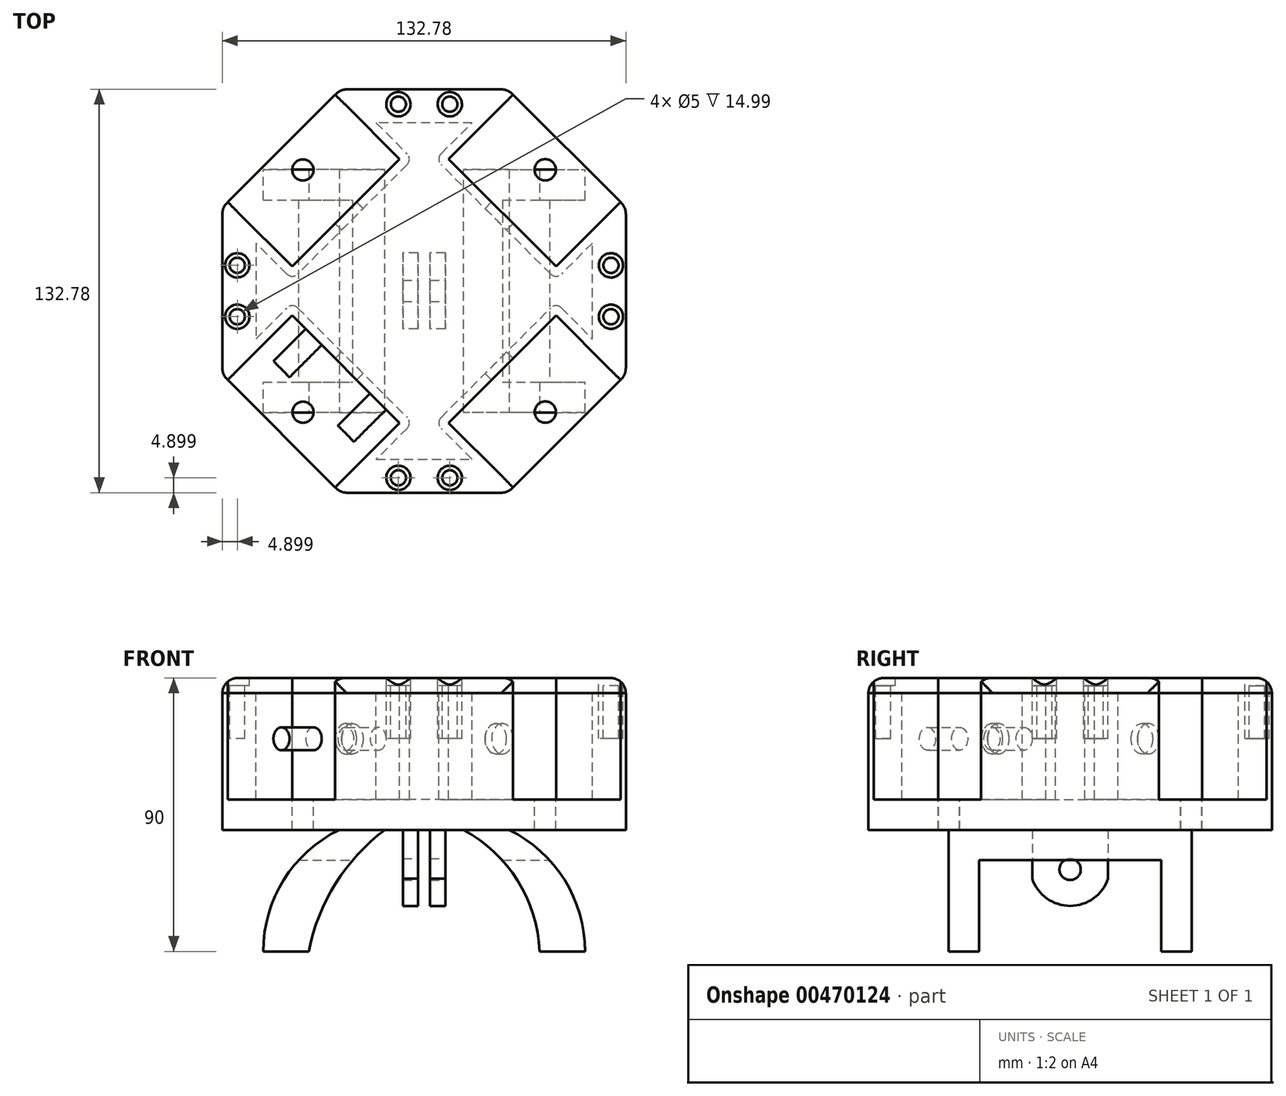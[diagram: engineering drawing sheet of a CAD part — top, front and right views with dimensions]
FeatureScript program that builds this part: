
annotation { "Feature Type Name" : "Feature", "Feature Type Description" : "" }
export const myFeature = defineFeature(function(context is Context, id is Id, definition is map)
    precondition{}
    {
        {
            var Q0;
            Q0=qCreatedBy(makeId("Top.planeOp"),FACE);
            var sketch = newSketch(context, id + "F0", { "sketchPlane" : qUnion([Q0])});
            skCircle(sketch, "E0.cCircle", {"center": v(0, 0) * mm, "radius": 71.86 * mm, "construction": true});
            skLineSegment(sketch, "E0.0", {"start": v(66.4, 27.5) * mm, "end": v(66.4, -27.5) * mm});
            skLineSegment(sketch, "E0.1", {"start": v(66.4, -27.5) * mm, "end": v(27.5, -66.4) * mm});
            skLineSegment(sketch, "E0.2", {"start": v(27.5, -66.4) * mm, "end": v(-27.5, -66.4) * mm});
            skLineSegment(sketch, "E0.3", {"start": v(-27.5, -66.4) * mm, "end": v(-66.4, -27.5) * mm});
            skLineSegment(sketch, "E0.4", {"start": v(-66.4, -27.5) * mm, "end": v(-66.4, 27.5) * mm});
            skLineSegment(sketch, "E0.5", {"start": v(-66.4, 27.5) * mm, "end": v(-27.5, 66.4) * mm});
            skLineSegment(sketch, "E0.6", {"start": v(-27.5, 66.4) * mm, "end": v(27.5, 66.4) * mm});
            skLineSegment(sketch, "E0.7", {"start": v(27.5, 66.4) * mm, "end": v(66.4, 27.5) * mm});
            skSolve(sketch);
        }
        {
            var Q0;
            Q0=makeQuery(id+"F0.imprint","IMPRINT",FACE,{"disambiguationData":[TD([[makeQuery(id+"F0.imprint","IMPRINT",EDGE,{"derivedFrom":sQuery(id+"F0.wireOp",EDGE,"E0.0")}),-1.0]])]});
            extrude(context, id + "F1", {"entities" : qUnion([Q0]), "depth" : 50 * mm});
        }
        {
            var Q0;
            Q0=makeQuery(id+"F1.opExtrude","CAP_FACE",FACE,{"disambiguationData":[OSD([sQuery(id+"F0.wireOp",EDGE,"E0.0"),sQuery(id+"F0.wireOp",EDGE,"E0.1"),sQuery(id+"F0.wireOp",EDGE,"E0.2"),sQuery(id+"F0.wireOp",EDGE,"E0.3"),sQuery(id+"F0.wireOp",EDGE,"E0.4"),sQuery(id+"F0.wireOp",EDGE,"E0.5"),sQuery(id+"F0.wireOp",EDGE,"E0.6"),sQuery(id+"F0.wireOp",EDGE,"E0.7")])],"isStart":true});
            var sketch = newSketch(context, id + "F2", { "sketchPlane" : qUnion([Q0])});
            skLineSegment(sketch, "E1", {"start": v(0, 66.4) * mm, "end": v(0, -66.4) * mm});
            skLineSegment(sketch, "E2.bottom", {"start": v(52.96, 40) * mm, "end": v(12.96, 40) * mm});
            skLineSegment(sketch, "E2.top", {"start": v(52.96, -40) * mm, "end": v(12.96, -40) * mm});
            skLineSegment(sketch, "E2.left", {"start": v(52.96, 40) * mm, "end": v(52.96, -40) * mm});
            skLineSegment(sketch, "E2.right", {"start": v(12.96, 40) * mm, "end": v(12.96, -40) * mm});
            skPoint(sketch, "E2.middle", {"position": v(32.96, 0) * mm});
            skLineSegment(sketch, "E3.MirrorCS", {"start": v(-12.96, 40) * mm, "end": v(-12.96, -40) * mm});
            skLineSegment(sketch, "E4.MirrorCS", {"start": v(-52.96, 40) * mm, "end": v(-12.96, 40) * mm});
            skLineSegment(sketch, "E5.MirrorCS", {"start": v(-52.96, 40) * mm, "end": v(-52.96, -40) * mm});
            skLineSegment(sketch, "E6.MirrorCS", {"start": v(-52.96, -40) * mm, "end": v(-12.96, -40) * mm});
            skSolve(sketch);
        }
        {
            var Q0;
            Q0 = qSketchRegion(id + "F2", true);
            extrude(context, id + "F3", {"entities" : qUnion([Q0]), "operationType" : NewBodyOperationType.ADD, "depth" : 40 * mm});
        }
        {
            var Q0;
            Q0=makeQuery(id+"F3.opExtrude","SWEPT_FACE",FACE,{"disambiguationData":[OSD([sQuery(id+"F2.wireOp",EDGE,"E2.bottom")])]});
            var sketch = newSketch(context, id + "F4", { "sketchPlane" : qUnion([Q0])});
            skArc(sketch, "E7", {"start": v(52.96, -40) * mm, "mid": v(46.2, -16.42) * mm, "end": v(27.96, 0) * mm});
            skArc(sketch, "E8", {"start": v(37.96, -40) * mm, "mid": v(30.79, -16.67) * mm, "end": v(12.96, 0) * mm});
            skLineSegment(sketch, "E9", {"start": v(0, 0) * mm, "end": v(0, -51.15) * mm});
            skArc(sketch, "E10.MirrorCS", {"start": v(-37.96, -40) * mm, "mid": v(-30.79, -16.67) * mm, "end": v(-12.96, 0) * mm});
            skArc(sketch, "E11.MirrorCS", {"start": v(-52.96, -40) * mm, "mid": v(-46.2, -16.42) * mm, "end": v(-27.96, 0) * mm});
            skLineSegment(sketch, "E12", {"start": v(-37.96, -40) * mm, "end": v(-52.96, -40) * mm});
            skLineSegment(sketch, "E13", {"start": v(-27.96, 0) * mm, "end": v(-12.96, 0) * mm});
            skSolve(sketch);
        }
        {
            var Q0;
            {var subQ0=sQuery(id+"F4.wireOp",EDGE,"E7");Q0=makeQuery(id+"F4.imprint","IMPRINT",FACE,{"disambiguationData":[TD([[makeQuery(id+"F4.imprint","IMPRINT",EDGE,{"derivedFrom":subQ0}),-1.0]])]});}
            var Q1;
            {var subQ0=sQuery(id+"F4.wireOp",EDGE,"E8");Q1=makeQuery(id+"F4.imprint","IMPRINT",FACE,{"disambiguationData":[TD([[makeQuery(id+"F4.imprint","IMPRINT",EDGE,{"derivedFrom":subQ0}),1.0]])]});}
            extrude(context, id + "F5", {"entities" : qUnion([Q0, Q1]), "operationType" : NewBodyOperationType.REMOVE, "endBound" : BoundingType.THROUGH_ALL, "oppositeDirection" : true, "depth" : 25 * mm});
        }
        {
            var Q0;
            Q0=makeQuery(id+"F3.opExtrude","SWEPT_FACE",FACE,{"disambiguationData":[OSD([sQuery(id+"F2.wireOp",EDGE,"E4.MirrorCS")])]});
            var sketch = newSketch(context, id + "F6", { "sketchPlane" : qUnion([Q0])});
            skArc(sketch, "E14", {"start": v(-27.96, 0) * mm, "mid": v(-46.2, -16.42) * mm, "end": v(-52.96, -40) * mm});
            skArc(sketch, "E15", {"start": v(-12.96, 0) * mm, "mid": v(-29.15, -17.7) * mm, "end": v(-37.96, -40) * mm});
            skSolve(sketch);
        }
        {
            var Q0;
            {var subQ0=sQuery(id+"F6.wireOp",EDGE,"E15");Q0=makeQuery(id+"F6.imprint","IMPRINT",FACE,{"disambiguationData":[TD([[makeQuery(id+"F6.imprint","IMPRINT",EDGE,{"derivedFrom":subQ0}),1.0]])]});}
            var Q1;
            {var subQ0=sQuery(id+"F6.wireOp",EDGE,"E14");Q1=makeQuery(id+"F6.imprint","IMPRINT",FACE,{"disambiguationData":[TD([[makeQuery(id+"F6.imprint","IMPRINT",EDGE,{"derivedFrom":subQ0}),-1.0]])]});}
            extrude(context, id + "F7", {"entities" : qUnion([Q0, Q1]), "operationType" : NewBodyOperationType.REMOVE, "endBound" : BoundingType.THROUGH_ALL, "oppositeDirection" : true, "depth" : 25 * mm});
        }
        {
            var Q0;
            Q0=makeQuery(id+"F3.opExtrude","CAP_FACE",FACE,{"disambiguationData":[OSD([sQuery(id+"F2.wireOp",EDGE,"E2.bottom"),sQuery(id+"F2.wireOp",EDGE,"E2.top"),sQuery(id+"F2.wireOp",EDGE,"E2.left"),sQuery(id+"F2.wireOp",EDGE,"E2.right")])],"isStart":false});
            extrude(context, id + "F8", {"entities" : qUnion([Q0]), "operationType" : NewBodyOperationType.ADD, "depth" : 10 * mm});
        }
        {
            var Q0;
            Q0=makeQuery(id+"F8.opExtrude","SWEPT_FACE",FACE,{"disambiguationData":[OSD([sQuery(id+"F2.wireOp",EDGE,"E2.bottom"),sQuery(id+"F2.wireOp",EDGE,"E2.left"),sQuery(id+"F4.wireOp",EDGE,"E7")])]});
            var sketch = newSketch(context, id + "F9", { "sketchPlane" : qUnion([Q0])});
            skLineSegment(sketch, "E16.bottom", {"start": v(-30, -50) * mm, "end": v(30, -50) * mm});
            skLineSegment(sketch, "E16.top", {"start": v(-30, -10) * mm, "end": v(30, -10) * mm});
            skLineSegment(sketch, "E16.left", {"start": v(-30, -50) * mm, "end": v(-30, -10) * mm});
            skLineSegment(sketch, "E16.right", {"start": v(30, -50) * mm, "end": v(30, -10) * mm});
            skLineSegment(sketch, "E17.bottom", {"start": v(-40, -40) * mm, "end": v(40, -40) * mm});
            skLineSegment(sketch, "E17.top", {"start": v(-40, -50) * mm, "end": v(40, -50) * mm});
            skLineSegment(sketch, "E17.left", {"start": v(-40, -40) * mm, "end": v(-40, -50) * mm});
            skLineSegment(sketch, "E17.right", {"start": v(40, -40) * mm, "end": v(40, -50) * mm});
            skSolve(sketch);
        }
        {
            var Q0;
            Q0 = qSketchRegion(id + "F9", true);
            extrude(context, id + "F10", {"entities" : qUnion([Q0]), "operationType" : NewBodyOperationType.REMOVE, "endBound" : BoundingType.THROUGH_ALL, "oppositeDirection" : true, "depth" : 25 * mm});
        }
        {
            var Q0;
            Q0=makeQuery(id+"F1.opExtrude","CAP_FACE",FACE,{"disambiguationData":[OSD([sQuery(id+"F0.wireOp",EDGE,"E0.0"),sQuery(id+"F0.wireOp",EDGE,"E0.1"),sQuery(id+"F0.wireOp",EDGE,"E0.2"),sQuery(id+"F0.wireOp",EDGE,"E0.3"),sQuery(id+"F0.wireOp",EDGE,"E0.4"),sQuery(id+"F0.wireOp",EDGE,"E0.5"),sQuery(id+"F0.wireOp",EDGE,"E0.6"),sQuery(id+"F0.wireOp",EDGE,"E0.7")])],"isStart":false});
            var sketch = newSketch(context, id + "F11", { "sketchPlane" : qUnion([Q0])});
            skLineSegment(sketch, "E18", {"start": v(29.27, -64.62) * mm, "end": v(8.05, -43.4) * mm});
            skLineSegment(sketch, "E19", {"start": v(64.62, -29.27) * mm, "end": v(43.4, -8.05) * mm});
            skLineSegment(sketch, "E20", {"start": v(8.05, -43.4) * mm, "end": v(43.4, -8.05) * mm});
            skLineSegment(sketch, "E21", {"start": v(43.4, 43.4) * mm, "end": v(-46.95, -46.95) * mm});
            skLineSegment(sketch, "E22", {"start": v(46.95, -46.95) * mm, "end": v(-46.95, 46.95) * mm});
            skLineSegment(sketch, "E23", {"start": v(-29.27, -64.62) * mm, "end": v(-8.05, -43.4) * mm});
            skLineSegment(sketch, "E24", {"start": v(-64.62, -29.27) * mm, "end": v(-43.4, -8.05) * mm});
            skLineSegment(sketch, "E25", {"start": v(-43.4, -8.05) * mm, "end": v(-8.05, -43.4) * mm});
            skLineSegment(sketch, "E26.MirrorCS", {"start": v(29.27, 64.62) * mm, "end": v(8.05, 43.4) * mm});
            skLineSegment(sketch, "E27.MirrorCS", {"start": v(8.05, 43.4) * mm, "end": v(43.4, 8.05) * mm});
            skLineSegment(sketch, "E28.MirrorCS", {"start": v(64.62, 29.27) * mm, "end": v(43.4, 8.05) * mm});
            skLineSegment(sketch, "E29.MirrorCS", {"start": v(-43.4, 8.05) * mm, "end": v(-8.05, 43.4) * mm});
            skLineSegment(sketch, "E30.MirrorCS", {"start": v(-29.27, 64.62) * mm, "end": v(-8.05, 43.4) * mm});
            skLineSegment(sketch, "E31", {"start": v(-43.4, 8.05) * mm, "end": v(-64.62, 29.27) * mm});
            skSolve(sketch);
        }
        {
            var Q0;
            {var subQ5=sQuery(id+"F11.wireOp",EDGE,"0e1623ae-2a34-4fe9-b9fa-2a8e952514210.MirrorCS");Q0=makeQuery(id+"F11.imprint","IMPRINT",FACE,{"disambiguationData":[TD([[makeQuery(id+"F11.imprint","IMPRINT",EDGE,{"derivedFrom":subQ5}),1.0]])]});}
            var Q1;
            {var subQ5=sQuery(id+"F11.wireOp",EDGE,"E30.MirrorCS");Q1=makeQuery(id+"F11.imprint","IMPRINT",FACE,{"disambiguationData":[TD([[makeQuery(id+"F11.imprint","IMPRINT",EDGE,{"derivedFrom":subQ5}),-1.0]])]});}
            var Q2;
            {var subQ5=sQuery(id+"F11.wireOp",EDGE,"E26.MirrorCS");Q2=makeQuery(id+"F11.imprint","IMPRINT",FACE,{"disambiguationData":[TD([[makeQuery(id+"F11.imprint","IMPRINT",EDGE,{"derivedFrom":subQ5}),1.0]])]});}
            var Q3;
            {var subQ5=sQuery(id+"F11.wireOp",EDGE,"E28.MirrorCS");Q3=makeQuery(id+"F11.imprint","IMPRINT",FACE,{"disambiguationData":[TD([[makeQuery(id+"F11.imprint","IMPRINT",EDGE,{"derivedFrom":subQ5}),-1.0]])]});}
            var Q4;
            {var subQ0=sQuery(id+"F11.wireOp",EDGE,"E19");Q4=makeQuery(id+"F11.imprint","IMPRINT",FACE,{"disambiguationData":[TD([[makeQuery(id+"F11.imprint","IMPRINT",EDGE,{"derivedFrom":subQ0}),1.0]])]});}
            var Q5;
            {var subQ0=sQuery(id+"F11.wireOp",EDGE,"E18");Q5=makeQuery(id+"F11.imprint","IMPRINT",FACE,{"disambiguationData":[TD([[makeQuery(id+"F11.imprint","IMPRINT",EDGE,{"derivedFrom":subQ0}),-1.0]])]});}
            var Q6;
            {var subQ5=sQuery(id+"F11.wireOp",EDGE,"E24");Q6=makeQuery(id+"F11.imprint","IMPRINT",FACE,{"disambiguationData":[TD([[makeQuery(id+"F11.imprint","IMPRINT",EDGE,{"derivedFrom":subQ5}),-1.0]])]});}
            var Q7;
            {var subQ5=sQuery(id+"F11.wireOp",EDGE,"E23");Q7=makeQuery(id+"F11.imprint","IMPRINT",FACE,{"disambiguationData":[TD([[makeQuery(id+"F11.imprint","IMPRINT",EDGE,{"derivedFrom":subQ5}),1.0]])]});}
            var Q8;
            {var subQ5=sQuery(id+"F11.wireOp",EDGE,"E31");Q8=makeQuery(id+"F11.imprint","IMPRINT",FACE,{"disambiguationData":[TD([[makeQuery(id+"F11.imprint","IMPRINT",EDGE,{"derivedFrom":subQ5}),-1.0]])]});}
            extrude(context, id + "F12", {"entities" : qUnion([Q0, Q1, Q2, Q3, Q4, Q5, Q6, Q7, Q8]), "operationType" : NewBodyOperationType.REMOVE, "oppositeDirection" : true, "depth" : 40 * mm});
        }
        {
            var Q0;
            {var subQ0=sQuery(id+"F2.wireOp",EDGE,"E4.MirrorCS");var subQ1=makeQuery(id+"F3.opExtrude","CAP_EDGE",EDGE,{"disambiguationData":[OSD([subQ0])],"isStart":true});var subQ2=sQuery(id+"F2.wireOp",EDGE,"E2.bottom");var subQ3=makeQuery(id+"F3.opExtrude","CAP_EDGE",EDGE,{"disambiguationData":[OSD([subQ2])],"isStart":true});Q0=makeQuery(id+"F7.boolean.opBoolean","MERGE",FACE,{"derivedFrom":[makeQuery(id+"F5.boolean.opBoolean","MERGE",FACE,{"derivedFrom":[makeQuery(id+"F1.opExtrude","CAP_FACE",FACE,{"disambiguationData":[OSD([sQuery(id+"F0.wireOp",EDGE,"E0.0"),sQuery(id+"F0.wireOp",EDGE,"E0.1"),sQuery(id+"F0.wireOp",EDGE,"E0.2"),sQuery(id+"F0.wireOp",EDGE,"E0.3"),sQuery(id+"F0.wireOp",EDGE,"E0.4"),sQuery(id+"F0.wireOp",EDGE,"E0.5"),sQuery(id+"F0.wireOp",EDGE,"E0.6"),sQuery(id+"F0.wireOp",EDGE,"E0.7")])],"isStart":true}),makeQuery(id+"F5.opExtrude","SWEPT_FACE",FACE,{"disambiguationData":[OSD([subQ2]),TDD([makeQuery(id+"F4.imprint","IMPRINT",EDGE,{"disambiguationData":[TD([[makeQuery(id+"F4.imprint","INTERSECT",VERTEX,{"derivedFrom":[subQ3,sQuery(id+"F4.wireOp",EDGE,"E7")]}),1.0]])],"derivedFrom":subQ3})])]})]}),makeQuery(id+"F7.opExtrude","SWEPT_FACE",FACE,{"disambiguationData":[OSD([subQ0]),TDD([makeQuery(id+"F6.imprint","IMPRINT",EDGE,{"disambiguationData":[TD([[makeQuery(id+"F6.imprint","INTERSECT",VERTEX,{"derivedFrom":[subQ1,sQuery(id+"F6.wireOp",EDGE,"E14")]}),1.0]])],"derivedFrom":subQ1})])]})]});}
            var sketch = newSketch(context, id + "F13", { "sketchPlane" : qUnion([Q0])});
            skLineSegment(sketch, "E32.bottom", {"start": v(10, 12.5) * mm, "end": v(-10, 12.5) * mm});
            skLineSegment(sketch, "E32.top", {"start": v(10, -12.5) * mm, "end": v(-10, -12.5) * mm});
            skLineSegment(sketch, "E32.left", {"start": v(10, 12.5) * mm, "end": v(10, -12.5) * mm});
            skLineSegment(sketch, "E32.right", {"start": v(-10, 12.5) * mm, "end": v(-10, -12.5) * mm});
            skPoint(sketch, "E32.middle", {"position": v(0, 0) * mm});
            skSolve(sketch);
        }
        {
            var Q0;
            Q0 = qSketchRegion(id + "F13", true);
            extrude(context, id + "F14", {"entities" : qUnion([Q0]), "operationType" : NewBodyOperationType.ADD, "depth" : 25 * mm});
        }
        {
            var Q0;
            Q0=makeQuery(id+"F14.opExtrude","CAP_FACE",FACE,{"disambiguationData":[OSD([sQuery(id+"F13.wireOp",EDGE,"E32.bottom"),sQuery(id+"F13.wireOp",EDGE,"E32.top"),sQuery(id+"F13.wireOp",EDGE,"E32.left"),sQuery(id+"F13.wireOp",EDGE,"E32.right")])],"isStart":false});
            var sketch = newSketch(context, id + "F15", { "sketchPlane" : qUnion([Q0])});
            skLineSegment(sketch, "E33.bottom", {"start": v(-7, 12.5) * mm, "end": v(-2, 12.5) * mm});
            skLineSegment(sketch, "E33.top", {"start": v(-7, -12.5) * mm, "end": v(-2, -12.5) * mm});
            skLineSegment(sketch, "E33.left", {"start": v(-7, 12.5) * mm, "end": v(-7, -12.5) * mm});
            skLineSegment(sketch, "E33.right", {"start": v(-2, 12.5) * mm, "end": v(-2, -12.5) * mm});
            skLineSegment(sketch, "E34.bottom", {"start": v(7, 12.5) * mm, "end": v(2, 12.5) * mm});
            skLineSegment(sketch, "E34.top", {"start": v(7, -12.5) * mm, "end": v(2, -12.5) * mm});
            skLineSegment(sketch, "E34.left", {"start": v(7, 12.5) * mm, "end": v(7, -12.5) * mm});
            skLineSegment(sketch, "E34.right", {"start": v(2, 12.5) * mm, "end": v(2, -12.5) * mm});
            skSolve(sketch);
        }
        {
            var Q0;
            Q0=makeQuery(id+"F14.opExtrude","SWEPT_FACE",FACE,{"disambiguationData":[OSD([sQuery(id+"F13.wireOp",EDGE,"E32.left")])]});
            var sketch = newSketch(context, id + "F16", { "sketchPlane" : qUnion([Q0])});
            skPoint(sketch, "E35", {"position": v(0, -25) * mm});
            skPoint(sketch, "E36", {"position": v(12.5, -16.09) * mm});
            skPoint(sketch, "E37", {"position": v(-12.5, -16.09) * mm});
            skArc(sketch, "E38", {"start": v(-12.5, -16.09) * mm, "mid": v(0, -25) * mm, "end": v(12.5, -16.09) * mm});
            skCircle(sketch, "E39", {"center": v(0, -13) * mm, "radius": 3.5 * mm});
            skSolve(sketch);
        }
        {
            var Q0;
            {var subQ0=sQuery(id+"F16.wireOp",EDGE,"E38");var subQ1=sQuery(id+"F13.wireOp",EDGE,"E32.left");var subQ4=makeQuery(id+"F14.opExtrude","CAP_EDGE",EDGE,{"disambiguationData":[OSD([subQ1])],"isStart":false});var subQ5=makeQuery(id+"F16.imprint","INTERSECT",VERTEX,{"derivedFrom":[subQ4,subQ0]});Q0=makeQuery(id+"F16.imprint","IMPRINT",FACE,{"disambiguationData":[TD([[makeQuery(id+"F16.imprint","IMPRINT",EDGE,{"disambiguationData":[TD([[subQ5,-1.0]])],"derivedFrom":subQ0}),-1.0]])]});}
            var Q1;
            {var subQ0=sQuery(id+"F16.wireOp",EDGE,"E38");var subQ1=sQuery(id+"F13.wireOp",EDGE,"E32.left");var subQ4=makeQuery(id+"F14.opExtrude","CAP_EDGE",EDGE,{"disambiguationData":[OSD([subQ1])],"isStart":false});var subQ5=makeQuery(id+"F16.imprint","INTERSECT",VERTEX,{"derivedFrom":[subQ4,subQ0]});Q1=makeQuery(id+"F16.imprint","IMPRINT",FACE,{"disambiguationData":[TD([[makeQuery(id+"F16.imprint","IMPRINT",EDGE,{"disambiguationData":[TD([[subQ5,1.0]])],"derivedFrom":subQ0}),-1.0]])]});}
            extrude(context, id + "F17", {"entities" : qUnion([Q0, Q1]), "operationType" : NewBodyOperationType.REMOVE, "endBound" : BoundingType.THROUGH_ALL, "oppositeDirection" : true, "depth" : 25 * mm});
        }
        {
            var Q0;
            {var subQ0=sQuery(id+"F15.wireOp",EDGE,"E34.left");Q0=makeQuery(id+"F15.imprint","IMPRINT",FACE,{"disambiguationData":[TD([[makeQuery(id+"F15.imprint","IMPRINT",EDGE,{"derivedFrom":subQ0}),1.0]])]});}
            var Q1;
            {var subQ0=sQuery(id+"F15.wireOp",EDGE,"E33.right");Q1=makeQuery(id+"F15.imprint","IMPRINT",FACE,{"disambiguationData":[TD([[makeQuery(id+"F15.imprint","IMPRINT",EDGE,{"derivedFrom":subQ0}),1.0]])]});}
            var Q2;
            {var subQ0=sQuery(id+"F15.wireOp",EDGE,"E33.left");Q2=makeQuery(id+"F15.imprint","IMPRINT",FACE,{"disambiguationData":[TD([[makeQuery(id+"F15.imprint","IMPRINT",EDGE,{"derivedFrom":subQ0}),-1.0]])]});}
            extrude(context, id + "F18", {"entities" : qUnion([Q0, Q1, Q2]), "operationType" : NewBodyOperationType.REMOVE, "oppositeDirection" : true, "depth" : 25 * mm});
        }
        {
            var Q0;
            Q0=makeQuery(id+"F12.boolean.opBoolean","COPY",FACE,{"derivedFrom":makeQuery(id+"F12.opExtrude","CAP_FACE",FACE,{"disambiguationData":[OSD([sQuery(id+"F0.wireOp",EDGE,"E0.1"),sQuery(id+"F11.wireOp",EDGE,"E18"),sQuery(id+"F11.wireOp",EDGE,"E19"),sQuery(id+"F11.wireOp",EDGE,"E20")])],"isStart":false})});
            var sketch = newSketch(context, id + "F19", { "sketchPlane" : qUnion([Q0])});
            skCircle(sketch, "E40", {"center": v(39.9, -39.85) * mm, "radius": 3.5 * mm});
            skSolve(sketch);
        }
        {
            var Q0;
            Q0 = qSketchRegion(id + "F16", true);
            extrude(context, id + "F20", {"entities" : qUnion([Q0]), "operationType" : NewBodyOperationType.REMOVE, "oppositeDirection" : true, "depth" : 25 * mm});
        }
        {
            var Q0;
            Q0=makeQuery(id+"F12.boolean.opBoolean","COPY",FACE,{"derivedFrom":makeQuery(id+"F12.opExtrude","CAP_FACE",FACE,{"disambiguationData":[OSD([sQuery(id+"F0.wireOp",EDGE,"E0.3"),sQuery(id+"F11.wireOp",EDGE,"E23"),sQuery(id+"F11.wireOp",EDGE,"E24"),sQuery(id+"F11.wireOp",EDGE,"E25")])],"isStart":false})});
            var sketch = newSketch(context, id + "F21", { "sketchPlane" : qUnion([Q0])});
            skCircle(sketch, "E41", {"center": v(-39.85, -39.9) * mm, "radius": 3.5 * mm});
            skSolve(sketch);
        }
        {
            var Q0;
            Q0=makeQuery(id+"F12.boolean.opBoolean","COPY",FACE,{"derivedFrom":makeQuery(id+"F12.opExtrude","CAP_FACE",FACE,{"disambiguationData":[OSD([sQuery(id+"F0.wireOp",EDGE,"E0.5"),sQuery(id+"F11.wireOp",EDGE,"E29.MirrorCS"),sQuery(id+"F11.wireOp",EDGE,"0e1623ae-2a34-4fe9-b9fa-2a8e952514210.MirrorCS"),sQuery(id+"F11.wireOp",EDGE,"E30.MirrorCS")])],"isStart":false})});
            var sketch = newSketch(context, id + "F22", { "sketchPlane" : qUnion([Q0])});
            skCircle(sketch, "E42", {"center": v(-39.9, 39.85) * mm, "radius": 3.5 * mm});
            skSolve(sketch);
        }
        {
            var Q0;
            Q0=makeQuery(id+"F12.boolean.opBoolean","COPY",FACE,{"derivedFrom":makeQuery(id+"F12.opExtrude","CAP_FACE",FACE,{"disambiguationData":[OSD([sQuery(id+"F0.wireOp",EDGE,"E0.7"),sQuery(id+"F11.wireOp",EDGE,"E26.MirrorCS"),sQuery(id+"F11.wireOp",EDGE,"E27.MirrorCS"),sQuery(id+"F11.wireOp",EDGE,"E28.MirrorCS")])],"isStart":false})});
            var sketch = newSketch(context, id + "F23", { "sketchPlane" : qUnion([Q0])});
            skCircle(sketch, "E43", {"center": v(39.85, 39.9) * mm, "radius": 3.5 * mm});
            skSolve(sketch);
        }
        {
            var Q0;
            Q0=makeQuery(id+"F22.imprint","IMPRINT",FACE,{"disambiguationData":[TD([[makeQuery(id+"F22.imprint","IMPRINT",EDGE,{"derivedFrom":sQuery(id+"F22.wireOp",EDGE,"E42")}),1.0]])]});
            var Q1;
            Q1=makeQuery(id+"F23.imprint","IMPRINT",FACE,{"disambiguationData":[TD([[makeQuery(id+"F23.imprint","IMPRINT",EDGE,{"derivedFrom":sQuery(id+"F23.wireOp",EDGE,"E43")}),1.0]])]});
            var Q2;
            Q2=makeQuery(id+"F19.imprint","IMPRINT",FACE,{"disambiguationData":[TD([[makeQuery(id+"F19.imprint","IMPRINT",EDGE,{"derivedFrom":sQuery(id+"F19.wireOp",EDGE,"E40")}),1.0]])]});
            var Q3;
            Q3=makeQuery(id+"F21.imprint","IMPRINT",FACE,{"disambiguationData":[TD([[makeQuery(id+"F21.imprint","IMPRINT",EDGE,{"derivedFrom":sQuery(id+"F21.wireOp",EDGE,"E41")}),1.0]])]});
            extrude(context, id + "F24", {"entities" : qUnion([Q0, Q1, Q2, Q3]), "operationType" : NewBodyOperationType.REMOVE, "oppositeDirection" : true, "depth" : 10 * mm});
        }
        {
            var Q0;
            Q0=makeQuery(id+"F1.opExtrude","CAP_EDGE",EDGE,{"disambiguationData":[OSD([sQuery(id+"F0.wireOp",EDGE,"E0.2")])],"isStart":false});
            var Q1;
            Q1=makeQuery(id+"F1.opExtrude","CAP_EDGE",EDGE,{"disambiguationData":[OSD([sQuery(id+"F0.wireOp",EDGE,"E0.0")])],"isStart":false});
            var Q2;
            Q2=makeQuery(id+"F1.opExtrude","CAP_EDGE",EDGE,{"disambiguationData":[OSD([sQuery(id+"F0.wireOp",EDGE,"E0.6")])],"isStart":false});
            var Q3;
            Q3=makeQuery(id+"F1.opExtrude","CAP_EDGE",EDGE,{"disambiguationData":[OSD([sQuery(id+"F0.wireOp",EDGE,"E0.4")])],"isStart":false});
            var Q4;
            Q4=makeQuery(id+"F1.opExtrude","SWEPT_EDGE",EDGE,{"disambiguationData":[OSD([sQuery(id+"F0.wireOp",EDGE,"E0.1"),sQuery(id+"F0.wireOp",EDGE,"E0.2")])]});
            var Q5;
            Q5=makeQuery(id+"F1.opExtrude","SWEPT_EDGE",EDGE,{"disambiguationData":[OSD([sQuery(id+"F0.wireOp",EDGE,"E0.2"),sQuery(id+"F0.wireOp",EDGE,"E0.3")])]});
            var Q6;
            Q6=makeQuery(id+"F1.opExtrude","SWEPT_EDGE",EDGE,{"disambiguationData":[OSD([sQuery(id+"F0.wireOp",EDGE,"E0.0"),sQuery(id+"F0.wireOp",EDGE,"E0.1")])]});
            var Q7;
            Q7=makeQuery(id+"F1.opExtrude","SWEPT_EDGE",EDGE,{"disambiguationData":[OSD([sQuery(id+"F0.wireOp",EDGE,"E0.0"),sQuery(id+"F0.wireOp",EDGE,"E0.7")])]});
            var Q8;
            Q8=makeQuery(id+"F1.opExtrude","SWEPT_EDGE",EDGE,{"disambiguationData":[OSD([sQuery(id+"F0.wireOp",EDGE,"E0.6"),sQuery(id+"F0.wireOp",EDGE,"E0.7")])]});
            var Q9;
            Q9=makeQuery(id+"F1.opExtrude","SWEPT_EDGE",EDGE,{"disambiguationData":[OSD([sQuery(id+"F0.wireOp",EDGE,"E0.4"),sQuery(id+"F0.wireOp",EDGE,"E0.5")])]});
            var Q10;
            Q10=makeQuery(id+"F1.opExtrude","SWEPT_EDGE",EDGE,{"disambiguationData":[OSD([sQuery(id+"F0.wireOp",EDGE,"E0.3"),sQuery(id+"F0.wireOp",EDGE,"E0.4")])]});
            var Q11;
            Q11=makeQuery(id+"F1.opExtrude","SWEPT_EDGE",EDGE,{"disambiguationData":[OSD([sQuery(id+"F0.wireOp",EDGE,"E0.5"),sQuery(id+"F0.wireOp",EDGE,"E0.6")])]});
            fillet(context, id + "F25", {"entities" : qUnion([Q0, Q1, Q2, Q3, Q4, Q5, Q6, Q7, Q8, Q9, Q10, Q11]), "radius" : 5 * mm, "tangentPropagation" : true, "allowEdgeOverflow" : false});
        }
        {
            var Q0;
            Q0=makeQuery(id+"F1.opExtrude","SWEPT_FACE",FACE,{"disambiguationData":[OSD([sQuery(id+"F0.wireOp",EDGE,"E0.2")])]});
            var sketch = newSketch(context, id + "F26", { "sketchPlane" : qUnion([Q0])});
            skLineSegment(sketch, "E44.bottom", {"start": v(90.93, 45) * mm, "end": v(-90.93, 45) * mm});
            skLineSegment(sketch, "E44.top", {"start": v(90.93, 44.99) * mm, "end": v(-90.93, 44.99) * mm});
            skLineSegment(sketch, "E44.left", {"start": v(90.93, 45) * mm, "end": v(90.93, 44.99) * mm});
            skLineSegment(sketch, "E44.right", {"start": v(-90.93, 45) * mm, "end": v(-90.93, 44.99) * mm});
            skPoint(sketch, "E44.middle", {"position": v(0, 45) * mm});
            skPoint(sketch, "E44.middle.positionSnap0", {"position": v(0, 45) * mm});
            skPoint(sketch, "E44.cornerSnap0", {"position": v(0, 45) * mm});
            skPoint(sketch, "E44.centerSnap0", {"position": v(0, 45) * mm});
            skSolve(sketch);
        }
        {
            var Q0;
            Q0 = qSketchRegion(id + "F26", true);
            extrude(context, id + "F27", {"entities" : qUnion([Q0]), "operationType" : NewBodyOperationType.REMOVE, "endBound" : BoundingType.THROUGH_ALL, "oppositeDirection" : true, "depth" : 25 * mm});
        }
        {
            var Q0;
            Q0=makeQuery(id+"F27.boolean.opBoolean","COPY",FACE,{"derivedFrom":makeQuery(id+"F27.opExtrude","SWEPT_FACE",FACE,{"disambiguationData":[OSD([sQuery(id+"F26.wireOp",EDGE,"E44.top")])]})});
            var sketch = newSketch(context, id + "F28", { "sketchPlane" : qUnion([Q0])});
            skLineSegment(sketch, "E45.0", {"start": v(-3.81, -43.4) * mm, "end": v(-23.8, -63.4) * mm});
            skLineSegment(sketch, "E45.1", {"start": v(-43.4, -3.81) * mm, "end": v(-3.81, -43.4) * mm});
            skLineSegment(sketch, "E45.2", {"start": v(-63.4, -23.8) * mm, "end": v(-43.4, -3.81) * mm});
            skLineSegment(sketch, "E45.3", {"start": v(-63.4, 23.8) * mm, "end": v(-63.4, -23.8) * mm});
            skLineSegment(sketch, "E45.4", {"start": v(-43.4, 3.81) * mm, "end": v(-63.4, 23.8) * mm});
            skLineSegment(sketch, "E45.5", {"start": v(63.4, -23.8) * mm, "end": v(63.4, 23.8) * mm});
            skLineSegment(sketch, "E45.6", {"start": v(43.4, -3.81) * mm, "end": v(63.4, -23.8) * mm});
            skLineSegment(sketch, "E45.7", {"start": v(3.81, -43.4) * mm, "end": v(43.4, -3.81) * mm});
            skLineSegment(sketch, "E45.8", {"start": v(23.8, -63.4) * mm, "end": v(3.81, -43.4) * mm});
            skLineSegment(sketch, "E45.9", {"start": v(63.4, 23.8) * mm, "end": v(43.4, 3.81) * mm});
            skLineSegment(sketch, "E45.10", {"start": v(43.4, 3.81) * mm, "end": v(3.81, 43.4) * mm});
            skLineSegment(sketch, "E45.11", {"start": v(3.81, 43.4) * mm, "end": v(23.8, 63.4) * mm});
            skLineSegment(sketch, "E45.12", {"start": v(23.8, 63.4) * mm, "end": v(-23.8, 63.4) * mm});
            skLineSegment(sketch, "E45.13", {"start": v(-23.8, 63.4) * mm, "end": v(-3.81, 43.4) * mm});
            skLineSegment(sketch, "E45.14", {"start": v(-23.8, -63.4) * mm, "end": v(23.8, -63.4) * mm});
            skLineSegment(sketch, "E45.15", {"start": v(-3.81, 43.4) * mm, "end": v(-43.4, 3.81) * mm});
            skLineSegment(sketch, "E46.0", {"start": v(15.8, 55.4) * mm, "end": v(-15.8, 55.4) * mm});
            skLineSegment(sketch, "E47.0", {"start": v(-55.4, 15.8) * mm, "end": v(-55.4, -15.8) * mm});
            skLineSegment(sketch, "E48.0", {"start": v(-15.8, -55.4) * mm, "end": v(15.8, -55.4) * mm});
            skLineSegment(sketch, "E49.0", {"start": v(55.4, -15.8) * mm, "end": v(55.4, 15.8) * mm});
            skSolve(sketch);
        }
        {
            var Q0;
            {var subQ1=sQuery(id+"F11.wireOp",EDGE,"E20");Q0=makeQuery(id+"F27.boolean.opBoolean","SPLIT",FACE,{"disambiguationData":[TD([makeQuery(id+"F27.opExtrude","SWEPT_FACE",FACE,{"disambiguationData":[OSD([sQuery(id+"F26.wireOp",EDGE,"E44.top")])]})])],"derivedFrom":makeQuery(id+"F12.boolean.opBoolean","COPY",FACE,{"derivedFrom":makeQuery(id+"F12.opExtrude","SWEPT_FACE",FACE,{"disambiguationData":[OSD([subQ1])]})})});}
            var sketch = newSketch(context, id + "F29", { "sketchPlane" : qUnion([Q0])});
            skCircle(sketch, "E50", {"center": v(0, 30) * mm, "radius": 5 * mm});
            skPoint(sketch, "E50.centerSnap0", {"position": v(0, 10) * mm});
            skSolve(sketch);
        }
        {
            var Q0;
            Q0 = qSketchRegion(id + "F29", true);
            extrude(context, id + "F30", {"entities" : qUnion([Q0]), "operationType" : NewBodyOperationType.REMOVE, "endBound" : BoundingType.THROUGH_ALL, "oppositeDirection" : true, "depth" : 25 * mm});
        }
        {
            var Q0;
            {var subQ1=sQuery(id+"F11.wireOp",EDGE,"E25");Q0=makeQuery(id+"F27.boolean.opBoolean","SPLIT",FACE,{"disambiguationData":[TD([makeQuery(id+"F27.opExtrude","SWEPT_FACE",FACE,{"disambiguationData":[OSD([sQuery(id+"F26.wireOp",EDGE,"E44.top")])]})])],"derivedFrom":makeQuery(id+"F12.boolean.opBoolean","COPY",FACE,{"derivedFrom":makeQuery(id+"F12.opExtrude","SWEPT_FACE",FACE,{"disambiguationData":[OSD([subQ1])]})})});}
            var sketch = newSketch(context, id + "F31", { "sketchPlane" : qUnion([Q0])});
            skCircle(sketch, "E51", {"center": v(0, 30) * mm, "radius": 5 * mm});
            skPoint(sketch, "E51.centerSnap0", {"position": v(0, 10) * mm});
            skCircle(sketch, "E52", {"center": v(15, 30) * mm, "radius": 3.75 * mm});
            skCircle(sketch, "E53", {"center": v(-15, 30) * mm, "radius": 3.75 * mm});
            skSolve(sketch);
        }
        {
            var Q0;
            Q0=makeQuery(id+"F31.imprint","IMPRINT",FACE,{"disambiguationData":[TD([[makeQuery(id+"F31.imprint","IMPRINT",EDGE,{"derivedFrom":sQuery(id+"F31.wireOp",EDGE,"E51")}),1.0]])]});
            extrude(context, id + "F32", {"entities" : qUnion([Q0]), "operationType" : NewBodyOperationType.REMOVE, "endBound" : BoundingType.THROUGH_ALL, "oppositeDirection" : true, "depth" : 25 * mm});
        }
        {
            var Q0;
            Q0=makeQuery(id+"F1.opExtrude","CAP_FACE",FACE,{"disambiguationData":[OSD([sQuery(id+"F0.wireOp",EDGE,"E0.0"),sQuery(id+"F0.wireOp",EDGE,"E0.1"),sQuery(id+"F0.wireOp",EDGE,"E0.2"),sQuery(id+"F0.wireOp",EDGE,"E0.3"),sQuery(id+"F0.wireOp",EDGE,"E0.4"),sQuery(id+"F0.wireOp",EDGE,"E0.5"),sQuery(id+"F0.wireOp",EDGE,"E0.6"),sQuery(id+"F0.wireOp",EDGE,"E0.7")])],"isStart":false});
            var sketch = newSketch(context, id + "F33", { "sketchPlane" : qUnion([Q0])});
            skCircle(sketch, "E54", {"center": v(-8.46, -61.5) * mm, "radius": 2.5 * mm});
            skCircle(sketch, "E55", {"center": v(8.46, -61.5) * mm, "radius": 2.5 * mm});
            skCircle(sketch, "E56.MirrorC", {"center": v(-8.46, 61.5) * mm, "radius": 2.5 * mm});
            skCircle(sketch, "E57.MirrorC", {"center": v(8.46, 61.5) * mm, "radius": 2.5 * mm});
            skCircle(sketch, "E58", {"center": v(-61.5, 8.46) * mm, "radius": 2.5 * mm});
            skCircle(sketch, "E59", {"center": v(-61.5, -8.46) * mm, "radius": 2.5 * mm});
            skCircle(sketch, "E60.MirrorC", {"center": v(61.5, 8.46) * mm, "radius": 2.5 * mm});
            skCircle(sketch, "E61.MirrorC", {"center": v(61.5, -8.46) * mm, "radius": 2.5 * mm});
            skCircle(sketch, "E62", {"center": v(-61.5, 8.46) * mm, "radius": 4 * mm});
            skCircle(sketch, "E63", {"center": v(-61.5, -8.46) * mm, "radius": 4 * mm});
            skCircle(sketch, "E64", {"center": v(-8.46, -61.5) * mm, "radius": 4 * mm});
            skCircle(sketch, "E65", {"center": v(8.46, -61.5) * mm, "radius": 4 * mm});
            skCircle(sketch, "E66", {"center": v(61.5, -8.46) * mm, "radius": 4 * mm});
            skCircle(sketch, "E67", {"center": v(61.5, 8.46) * mm, "radius": 4 * mm});
            skCircle(sketch, "E68", {"center": v(8.46, 61.5) * mm, "radius": 4 * mm});
            skCircle(sketch, "E69", {"center": v(-8.46, 61.5) * mm, "radius": 4 * mm});
            skSolve(sketch);
        }
        {
            var Q0;
            {var subQ0=sQuery(id+"F33.wireOp",EDGE,"E56.MirrorC");var subQ1=sQuery(id+"F0.wireOp",EDGE,"E0.6");var subQ2=makeQuery(id+"F25.opFillet","BLEND_EDGE",EDGE,{"blendedFrom":[makeQuery(id+"F1.opExtrude","CAP_EDGE",EDGE,{"disambiguationData":[OSD([subQ1])],"isStart":false}),makeQuery(id+"F1.opExtrude","CAP_FACE",FACE,{"disambiguationData":[OSD([sQuery(id+"F0.wireOp",EDGE,"E0.0"),sQuery(id+"F0.wireOp",EDGE,"E0.1"),sQuery(id+"F0.wireOp",EDGE,"E0.2"),sQuery(id+"F0.wireOp",EDGE,"E0.3"),sQuery(id+"F0.wireOp",EDGE,"E0.4"),sQuery(id+"F0.wireOp",EDGE,"E0.5"),subQ1,sQuery(id+"F0.wireOp",EDGE,"E0.7")])],"isStart":false})],"blendedInto":[makeQuery(id+"F1.opExtrude","CAP_FACE",FACE,{"disambiguationData":[OSD([sQuery(id+"F0.wireOp",EDGE,"E0.0"),sQuery(id+"F0.wireOp",EDGE,"E0.1"),sQuery(id+"F0.wireOp",EDGE,"E0.2"),sQuery(id+"F0.wireOp",EDGE,"E0.3"),sQuery(id+"F0.wireOp",EDGE,"E0.4"),sQuery(id+"F0.wireOp",EDGE,"E0.5"),subQ1,sQuery(id+"F0.wireOp",EDGE,"E0.7")])],"isStart":false})]});var subQ3=makeQuery(id+"F33.imprint","INTERSECT",VERTEX,{"disambiguationData":[OD(0.0)],"derivedFrom":[subQ2,subQ0]});Q0=makeQuery(id+"F33.imprint","IMPRINT",FACE,{"disambiguationData":[TD([[makeQuery(id+"F33.imprint","IMPRINT",EDGE,{"disambiguationData":[TD([[subQ3,-1.0]])],"derivedFrom":subQ0}),-1.0]])]});}
            var Q1;
            {var subQ0=sQuery(id+"F33.wireOp",EDGE,"E56.MirrorC");var subQ1=sQuery(id+"F0.wireOp",EDGE,"E0.6");var subQ2=makeQuery(id+"F25.opFillet","BLEND_EDGE",EDGE,{"blendedFrom":[makeQuery(id+"F1.opExtrude","CAP_EDGE",EDGE,{"disambiguationData":[OSD([subQ1])],"isStart":false}),makeQuery(id+"F1.opExtrude","CAP_FACE",FACE,{"disambiguationData":[OSD([sQuery(id+"F0.wireOp",EDGE,"E0.0"),sQuery(id+"F0.wireOp",EDGE,"E0.1"),sQuery(id+"F0.wireOp",EDGE,"E0.2"),sQuery(id+"F0.wireOp",EDGE,"E0.3"),sQuery(id+"F0.wireOp",EDGE,"E0.4"),sQuery(id+"F0.wireOp",EDGE,"E0.5"),subQ1,sQuery(id+"F0.wireOp",EDGE,"E0.7")])],"isStart":false})],"blendedInto":[makeQuery(id+"F1.opExtrude","CAP_FACE",FACE,{"disambiguationData":[OSD([sQuery(id+"F0.wireOp",EDGE,"E0.0"),sQuery(id+"F0.wireOp",EDGE,"E0.1"),sQuery(id+"F0.wireOp",EDGE,"E0.2"),sQuery(id+"F0.wireOp",EDGE,"E0.3"),sQuery(id+"F0.wireOp",EDGE,"E0.4"),sQuery(id+"F0.wireOp",EDGE,"E0.5"),subQ1,sQuery(id+"F0.wireOp",EDGE,"E0.7")])],"isStart":false})]});var subQ3=makeQuery(id+"F33.imprint","INTERSECT",VERTEX,{"disambiguationData":[OD(0.0)],"derivedFrom":[subQ2,subQ0]});Q1=makeQuery(id+"F33.imprint","IMPRINT",FACE,{"disambiguationData":[TD([[makeQuery(id+"F33.imprint","IMPRINT",EDGE,{"disambiguationData":[TD([[subQ3,1.0]])],"derivedFrom":subQ0}),-1.0]])]});}
            var Q2;
            {var subQ0=sQuery(id+"F33.wireOp",EDGE,"E57.MirrorC");var subQ1=sQuery(id+"F0.wireOp",EDGE,"E0.6");var subQ2=makeQuery(id+"F25.opFillet","BLEND_EDGE",EDGE,{"blendedFrom":[makeQuery(id+"F1.opExtrude","CAP_EDGE",EDGE,{"disambiguationData":[OSD([subQ1])],"isStart":false}),makeQuery(id+"F1.opExtrude","CAP_FACE",FACE,{"disambiguationData":[OSD([sQuery(id+"F0.wireOp",EDGE,"E0.0"),sQuery(id+"F0.wireOp",EDGE,"E0.1"),sQuery(id+"F0.wireOp",EDGE,"E0.2"),sQuery(id+"F0.wireOp",EDGE,"E0.3"),sQuery(id+"F0.wireOp",EDGE,"E0.4"),sQuery(id+"F0.wireOp",EDGE,"E0.5"),subQ1,sQuery(id+"F0.wireOp",EDGE,"E0.7")])],"isStart":false})],"blendedInto":[makeQuery(id+"F1.opExtrude","CAP_FACE",FACE,{"disambiguationData":[OSD([sQuery(id+"F0.wireOp",EDGE,"E0.0"),sQuery(id+"F0.wireOp",EDGE,"E0.1"),sQuery(id+"F0.wireOp",EDGE,"E0.2"),sQuery(id+"F0.wireOp",EDGE,"E0.3"),sQuery(id+"F0.wireOp",EDGE,"E0.4"),sQuery(id+"F0.wireOp",EDGE,"E0.5"),subQ1,sQuery(id+"F0.wireOp",EDGE,"E0.7")])],"isStart":false})]});var subQ3=makeQuery(id+"F33.imprint","INTERSECT",VERTEX,{"disambiguationData":[OD(0.0)],"derivedFrom":[subQ2,subQ0]});Q2=makeQuery(id+"F33.imprint","IMPRINT",FACE,{"disambiguationData":[TD([[makeQuery(id+"F33.imprint","IMPRINT",EDGE,{"disambiguationData":[TD([[subQ3,1.0]])],"derivedFrom":subQ0}),-1.0]])]});}
            var Q3;
            {var subQ0=sQuery(id+"F33.wireOp",EDGE,"E57.MirrorC");var subQ1=sQuery(id+"F0.wireOp",EDGE,"E0.6");var subQ2=makeQuery(id+"F25.opFillet","BLEND_EDGE",EDGE,{"blendedFrom":[makeQuery(id+"F1.opExtrude","CAP_EDGE",EDGE,{"disambiguationData":[OSD([subQ1])],"isStart":false}),makeQuery(id+"F1.opExtrude","CAP_FACE",FACE,{"disambiguationData":[OSD([sQuery(id+"F0.wireOp",EDGE,"E0.0"),sQuery(id+"F0.wireOp",EDGE,"E0.1"),sQuery(id+"F0.wireOp",EDGE,"E0.2"),sQuery(id+"F0.wireOp",EDGE,"E0.3"),sQuery(id+"F0.wireOp",EDGE,"E0.4"),sQuery(id+"F0.wireOp",EDGE,"E0.5"),subQ1,sQuery(id+"F0.wireOp",EDGE,"E0.7")])],"isStart":false})],"blendedInto":[makeQuery(id+"F1.opExtrude","CAP_FACE",FACE,{"disambiguationData":[OSD([sQuery(id+"F0.wireOp",EDGE,"E0.0"),sQuery(id+"F0.wireOp",EDGE,"E0.1"),sQuery(id+"F0.wireOp",EDGE,"E0.2"),sQuery(id+"F0.wireOp",EDGE,"E0.3"),sQuery(id+"F0.wireOp",EDGE,"E0.4"),sQuery(id+"F0.wireOp",EDGE,"E0.5"),subQ1,sQuery(id+"F0.wireOp",EDGE,"E0.7")])],"isStart":false})]});var subQ3=makeQuery(id+"F33.imprint","INTERSECT",VERTEX,{"disambiguationData":[OD(0.0)],"derivedFrom":[subQ2,subQ0]});Q3=makeQuery(id+"F33.imprint","IMPRINT",FACE,{"disambiguationData":[TD([[makeQuery(id+"F33.imprint","IMPRINT",EDGE,{"disambiguationData":[TD([[subQ3,-1.0]])],"derivedFrom":subQ0}),-1.0]])]});}
            var Q4;
            {var subQ0=sQuery(id+"F33.wireOp",EDGE,"E58");var subQ1=sQuery(id+"F0.wireOp",EDGE,"E0.4");var subQ2=makeQuery(id+"F25.opFillet","BLEND_EDGE",EDGE,{"blendedFrom":[makeQuery(id+"F1.opExtrude","CAP_EDGE",EDGE,{"disambiguationData":[OSD([subQ1])],"isStart":false}),makeQuery(id+"F1.opExtrude","CAP_FACE",FACE,{"disambiguationData":[OSD([sQuery(id+"F0.wireOp",EDGE,"E0.0"),sQuery(id+"F0.wireOp",EDGE,"E0.1"),sQuery(id+"F0.wireOp",EDGE,"E0.2"),sQuery(id+"F0.wireOp",EDGE,"E0.3"),subQ1,sQuery(id+"F0.wireOp",EDGE,"E0.5"),sQuery(id+"F0.wireOp",EDGE,"E0.6"),sQuery(id+"F0.wireOp",EDGE,"E0.7")])],"isStart":false})],"blendedInto":[makeQuery(id+"F1.opExtrude","CAP_FACE",FACE,{"disambiguationData":[OSD([sQuery(id+"F0.wireOp",EDGE,"E0.0"),sQuery(id+"F0.wireOp",EDGE,"E0.1"),sQuery(id+"F0.wireOp",EDGE,"E0.2"),sQuery(id+"F0.wireOp",EDGE,"E0.3"),subQ1,sQuery(id+"F0.wireOp",EDGE,"E0.5"),sQuery(id+"F0.wireOp",EDGE,"E0.6"),sQuery(id+"F0.wireOp",EDGE,"E0.7")])],"isStart":false})]});var subQ3=makeQuery(id+"F33.imprint","INTERSECT",VERTEX,{"disambiguationData":[OD(0.0)],"derivedFrom":[subQ2,subQ0]});Q4=makeQuery(id+"F33.imprint","IMPRINT",FACE,{"disambiguationData":[TD([[makeQuery(id+"F33.imprint","IMPRINT",EDGE,{"disambiguationData":[TD([[subQ3,-1.0]])],"derivedFrom":subQ0}),1.0]])]});}
            var Q5;
            {var subQ0=sQuery(id+"F33.wireOp",EDGE,"E58");var subQ1=sQuery(id+"F0.wireOp",EDGE,"E0.4");var subQ2=makeQuery(id+"F25.opFillet","BLEND_EDGE",EDGE,{"blendedFrom":[makeQuery(id+"F1.opExtrude","CAP_EDGE",EDGE,{"disambiguationData":[OSD([subQ1])],"isStart":false}),makeQuery(id+"F1.opExtrude","CAP_FACE",FACE,{"disambiguationData":[OSD([sQuery(id+"F0.wireOp",EDGE,"E0.0"),sQuery(id+"F0.wireOp",EDGE,"E0.1"),sQuery(id+"F0.wireOp",EDGE,"E0.2"),sQuery(id+"F0.wireOp",EDGE,"E0.3"),subQ1,sQuery(id+"F0.wireOp",EDGE,"E0.5"),sQuery(id+"F0.wireOp",EDGE,"E0.6"),sQuery(id+"F0.wireOp",EDGE,"E0.7")])],"isStart":false})],"blendedInto":[makeQuery(id+"F1.opExtrude","CAP_FACE",FACE,{"disambiguationData":[OSD([sQuery(id+"F0.wireOp",EDGE,"E0.0"),sQuery(id+"F0.wireOp",EDGE,"E0.1"),sQuery(id+"F0.wireOp",EDGE,"E0.2"),sQuery(id+"F0.wireOp",EDGE,"E0.3"),subQ1,sQuery(id+"F0.wireOp",EDGE,"E0.5"),sQuery(id+"F0.wireOp",EDGE,"E0.6"),sQuery(id+"F0.wireOp",EDGE,"E0.7")])],"isStart":false})]});var subQ3=makeQuery(id+"F33.imprint","INTERSECT",VERTEX,{"disambiguationData":[OD(0.0)],"derivedFrom":[subQ2,subQ0]});Q5=makeQuery(id+"F33.imprint","IMPRINT",FACE,{"disambiguationData":[TD([[makeQuery(id+"F33.imprint","IMPRINT",EDGE,{"disambiguationData":[TD([[subQ3,1.0]])],"derivedFrom":subQ0}),1.0]])]});}
            var Q6;
            {var subQ0=sQuery(id+"F33.wireOp",EDGE,"E59");var subQ1=sQuery(id+"F0.wireOp",EDGE,"E0.4");var subQ2=makeQuery(id+"F25.opFillet","BLEND_EDGE",EDGE,{"blendedFrom":[makeQuery(id+"F1.opExtrude","CAP_EDGE",EDGE,{"disambiguationData":[OSD([subQ1])],"isStart":false}),makeQuery(id+"F1.opExtrude","CAP_FACE",FACE,{"disambiguationData":[OSD([sQuery(id+"F0.wireOp",EDGE,"E0.0"),sQuery(id+"F0.wireOp",EDGE,"E0.1"),sQuery(id+"F0.wireOp",EDGE,"E0.2"),sQuery(id+"F0.wireOp",EDGE,"E0.3"),subQ1,sQuery(id+"F0.wireOp",EDGE,"E0.5"),sQuery(id+"F0.wireOp",EDGE,"E0.6"),sQuery(id+"F0.wireOp",EDGE,"E0.7")])],"isStart":false})],"blendedInto":[makeQuery(id+"F1.opExtrude","CAP_FACE",FACE,{"disambiguationData":[OSD([sQuery(id+"F0.wireOp",EDGE,"E0.0"),sQuery(id+"F0.wireOp",EDGE,"E0.1"),sQuery(id+"F0.wireOp",EDGE,"E0.2"),sQuery(id+"F0.wireOp",EDGE,"E0.3"),subQ1,sQuery(id+"F0.wireOp",EDGE,"E0.5"),sQuery(id+"F0.wireOp",EDGE,"E0.6"),sQuery(id+"F0.wireOp",EDGE,"E0.7")])],"isStart":false})]});var subQ3=makeQuery(id+"F33.imprint","INTERSECT",VERTEX,{"disambiguationData":[OD(0.0)],"derivedFrom":[subQ2,subQ0]});Q6=makeQuery(id+"F33.imprint","IMPRINT",FACE,{"disambiguationData":[TD([[makeQuery(id+"F33.imprint","IMPRINT",EDGE,{"disambiguationData":[TD([[subQ3,1.0]])],"derivedFrom":subQ0}),1.0]])]});}
            var Q7;
            {var subQ0=sQuery(id+"F33.wireOp",EDGE,"E59");var subQ1=sQuery(id+"F0.wireOp",EDGE,"E0.4");var subQ2=makeQuery(id+"F25.opFillet","BLEND_EDGE",EDGE,{"blendedFrom":[makeQuery(id+"F1.opExtrude","CAP_EDGE",EDGE,{"disambiguationData":[OSD([subQ1])],"isStart":false}),makeQuery(id+"F1.opExtrude","CAP_FACE",FACE,{"disambiguationData":[OSD([sQuery(id+"F0.wireOp",EDGE,"E0.0"),sQuery(id+"F0.wireOp",EDGE,"E0.1"),sQuery(id+"F0.wireOp",EDGE,"E0.2"),sQuery(id+"F0.wireOp",EDGE,"E0.3"),subQ1,sQuery(id+"F0.wireOp",EDGE,"E0.5"),sQuery(id+"F0.wireOp",EDGE,"E0.6"),sQuery(id+"F0.wireOp",EDGE,"E0.7")])],"isStart":false})],"blendedInto":[makeQuery(id+"F1.opExtrude","CAP_FACE",FACE,{"disambiguationData":[OSD([sQuery(id+"F0.wireOp",EDGE,"E0.0"),sQuery(id+"F0.wireOp",EDGE,"E0.1"),sQuery(id+"F0.wireOp",EDGE,"E0.2"),sQuery(id+"F0.wireOp",EDGE,"E0.3"),subQ1,sQuery(id+"F0.wireOp",EDGE,"E0.5"),sQuery(id+"F0.wireOp",EDGE,"E0.6"),sQuery(id+"F0.wireOp",EDGE,"E0.7")])],"isStart":false})]});var subQ3=makeQuery(id+"F33.imprint","INTERSECT",VERTEX,{"disambiguationData":[OD(0.0)],"derivedFrom":[subQ2,subQ0]});Q7=makeQuery(id+"F33.imprint","IMPRINT",FACE,{"disambiguationData":[TD([[makeQuery(id+"F33.imprint","IMPRINT",EDGE,{"disambiguationData":[TD([[subQ3,-1.0]])],"derivedFrom":subQ0}),1.0]])]});}
            var Q8;
            {var subQ0=sQuery(id+"F33.wireOp",EDGE,"E61.MirrorC");var subQ1=sQuery(id+"F0.wireOp",EDGE,"E0.0");var subQ2=makeQuery(id+"F25.opFillet","BLEND_EDGE",EDGE,{"blendedFrom":[makeQuery(id+"F1.opExtrude","CAP_EDGE",EDGE,{"disambiguationData":[OSD([subQ1])],"isStart":false}),makeQuery(id+"F1.opExtrude","CAP_FACE",FACE,{"disambiguationData":[OSD([subQ1,sQuery(id+"F0.wireOp",EDGE,"E0.1"),sQuery(id+"F0.wireOp",EDGE,"E0.2"),sQuery(id+"F0.wireOp",EDGE,"E0.3"),sQuery(id+"F0.wireOp",EDGE,"E0.4"),sQuery(id+"F0.wireOp",EDGE,"E0.5"),sQuery(id+"F0.wireOp",EDGE,"E0.6"),sQuery(id+"F0.wireOp",EDGE,"E0.7")])],"isStart":false})],"blendedInto":[makeQuery(id+"F1.opExtrude","CAP_FACE",FACE,{"disambiguationData":[OSD([subQ1,sQuery(id+"F0.wireOp",EDGE,"E0.1"),sQuery(id+"F0.wireOp",EDGE,"E0.2"),sQuery(id+"F0.wireOp",EDGE,"E0.3"),sQuery(id+"F0.wireOp",EDGE,"E0.4"),sQuery(id+"F0.wireOp",EDGE,"E0.5"),sQuery(id+"F0.wireOp",EDGE,"E0.6"),sQuery(id+"F0.wireOp",EDGE,"E0.7")])],"isStart":false})]});var subQ3=makeQuery(id+"F33.imprint","INTERSECT",VERTEX,{"disambiguationData":[OD(0.0)],"derivedFrom":[subQ2,subQ0]});Q8=makeQuery(id+"F33.imprint","IMPRINT",FACE,{"disambiguationData":[TD([[makeQuery(id+"F33.imprint","IMPRINT",EDGE,{"disambiguationData":[TD([[subQ3,-1.0]])],"derivedFrom":subQ0}),-1.0]])]});}
            var Q9;
            {var subQ0=sQuery(id+"F33.wireOp",EDGE,"E61.MirrorC");var subQ1=sQuery(id+"F0.wireOp",EDGE,"E0.0");var subQ2=makeQuery(id+"F25.opFillet","BLEND_EDGE",EDGE,{"blendedFrom":[makeQuery(id+"F1.opExtrude","CAP_EDGE",EDGE,{"disambiguationData":[OSD([subQ1])],"isStart":false}),makeQuery(id+"F1.opExtrude","CAP_FACE",FACE,{"disambiguationData":[OSD([subQ1,sQuery(id+"F0.wireOp",EDGE,"E0.1"),sQuery(id+"F0.wireOp",EDGE,"E0.2"),sQuery(id+"F0.wireOp",EDGE,"E0.3"),sQuery(id+"F0.wireOp",EDGE,"E0.4"),sQuery(id+"F0.wireOp",EDGE,"E0.5"),sQuery(id+"F0.wireOp",EDGE,"E0.6"),sQuery(id+"F0.wireOp",EDGE,"E0.7")])],"isStart":false})],"blendedInto":[makeQuery(id+"F1.opExtrude","CAP_FACE",FACE,{"disambiguationData":[OSD([subQ1,sQuery(id+"F0.wireOp",EDGE,"E0.1"),sQuery(id+"F0.wireOp",EDGE,"E0.2"),sQuery(id+"F0.wireOp",EDGE,"E0.3"),sQuery(id+"F0.wireOp",EDGE,"E0.4"),sQuery(id+"F0.wireOp",EDGE,"E0.5"),sQuery(id+"F0.wireOp",EDGE,"E0.6"),sQuery(id+"F0.wireOp",EDGE,"E0.7")])],"isStart":false})]});var subQ3=makeQuery(id+"F33.imprint","INTERSECT",VERTEX,{"disambiguationData":[OD(0.0)],"derivedFrom":[subQ2,subQ0]});Q9=makeQuery(id+"F33.imprint","IMPRINT",FACE,{"disambiguationData":[TD([[makeQuery(id+"F33.imprint","IMPRINT",EDGE,{"disambiguationData":[TD([[subQ3,1.0]])],"derivedFrom":subQ0}),-1.0]])]});}
            var Q10;
            {var subQ0=sQuery(id+"F33.wireOp",EDGE,"E60.MirrorC");var subQ1=sQuery(id+"F0.wireOp",EDGE,"E0.0");var subQ2=makeQuery(id+"F25.opFillet","BLEND_EDGE",EDGE,{"blendedFrom":[makeQuery(id+"F1.opExtrude","CAP_EDGE",EDGE,{"disambiguationData":[OSD([subQ1])],"isStart":false}),makeQuery(id+"F1.opExtrude","CAP_FACE",FACE,{"disambiguationData":[OSD([subQ1,sQuery(id+"F0.wireOp",EDGE,"E0.1"),sQuery(id+"F0.wireOp",EDGE,"E0.2"),sQuery(id+"F0.wireOp",EDGE,"E0.3"),sQuery(id+"F0.wireOp",EDGE,"E0.4"),sQuery(id+"F0.wireOp",EDGE,"E0.5"),sQuery(id+"F0.wireOp",EDGE,"E0.6"),sQuery(id+"F0.wireOp",EDGE,"E0.7")])],"isStart":false})],"blendedInto":[makeQuery(id+"F1.opExtrude","CAP_FACE",FACE,{"disambiguationData":[OSD([subQ1,sQuery(id+"F0.wireOp",EDGE,"E0.1"),sQuery(id+"F0.wireOp",EDGE,"E0.2"),sQuery(id+"F0.wireOp",EDGE,"E0.3"),sQuery(id+"F0.wireOp",EDGE,"E0.4"),sQuery(id+"F0.wireOp",EDGE,"E0.5"),sQuery(id+"F0.wireOp",EDGE,"E0.6"),sQuery(id+"F0.wireOp",EDGE,"E0.7")])],"isStart":false})]});var subQ3=makeQuery(id+"F33.imprint","INTERSECT",VERTEX,{"disambiguationData":[OD(0.0)],"derivedFrom":[subQ2,subQ0]});Q10=makeQuery(id+"F33.imprint","IMPRINT",FACE,{"disambiguationData":[TD([[makeQuery(id+"F33.imprint","IMPRINT",EDGE,{"disambiguationData":[TD([[subQ3,-1.0]])],"derivedFrom":subQ0}),-1.0]])]});}
            var Q11;
            {var subQ0=sQuery(id+"F33.wireOp",EDGE,"E60.MirrorC");var subQ1=sQuery(id+"F0.wireOp",EDGE,"E0.0");var subQ2=makeQuery(id+"F25.opFillet","BLEND_EDGE",EDGE,{"blendedFrom":[makeQuery(id+"F1.opExtrude","CAP_EDGE",EDGE,{"disambiguationData":[OSD([subQ1])],"isStart":false}),makeQuery(id+"F1.opExtrude","CAP_FACE",FACE,{"disambiguationData":[OSD([subQ1,sQuery(id+"F0.wireOp",EDGE,"E0.1"),sQuery(id+"F0.wireOp",EDGE,"E0.2"),sQuery(id+"F0.wireOp",EDGE,"E0.3"),sQuery(id+"F0.wireOp",EDGE,"E0.4"),sQuery(id+"F0.wireOp",EDGE,"E0.5"),sQuery(id+"F0.wireOp",EDGE,"E0.6"),sQuery(id+"F0.wireOp",EDGE,"E0.7")])],"isStart":false})],"blendedInto":[makeQuery(id+"F1.opExtrude","CAP_FACE",FACE,{"disambiguationData":[OSD([subQ1,sQuery(id+"F0.wireOp",EDGE,"E0.1"),sQuery(id+"F0.wireOp",EDGE,"E0.2"),sQuery(id+"F0.wireOp",EDGE,"E0.3"),sQuery(id+"F0.wireOp",EDGE,"E0.4"),sQuery(id+"F0.wireOp",EDGE,"E0.5"),sQuery(id+"F0.wireOp",EDGE,"E0.6"),sQuery(id+"F0.wireOp",EDGE,"E0.7")])],"isStart":false})]});var subQ3=makeQuery(id+"F33.imprint","INTERSECT",VERTEX,{"disambiguationData":[OD(0.0)],"derivedFrom":[subQ2,subQ0]});Q11=makeQuery(id+"F33.imprint","IMPRINT",FACE,{"disambiguationData":[TD([[makeQuery(id+"F33.imprint","IMPRINT",EDGE,{"disambiguationData":[TD([[subQ3,1.0]])],"derivedFrom":subQ0}),-1.0]])]});}
            var Q12;
            {var subQ0=sQuery(id+"F33.wireOp",EDGE,"E54");var subQ1=sQuery(id+"F0.wireOp",EDGE,"E0.2");var subQ2=makeQuery(id+"F25.opFillet","BLEND_EDGE",EDGE,{"blendedFrom":[makeQuery(id+"F1.opExtrude","CAP_EDGE",EDGE,{"disambiguationData":[OSD([subQ1])],"isStart":false}),makeQuery(id+"F1.opExtrude","CAP_FACE",FACE,{"disambiguationData":[OSD([sQuery(id+"F0.wireOp",EDGE,"E0.0"),sQuery(id+"F0.wireOp",EDGE,"E0.1"),subQ1,sQuery(id+"F0.wireOp",EDGE,"E0.3"),sQuery(id+"F0.wireOp",EDGE,"E0.4"),sQuery(id+"F0.wireOp",EDGE,"E0.5"),sQuery(id+"F0.wireOp",EDGE,"E0.6"),sQuery(id+"F0.wireOp",EDGE,"E0.7")])],"isStart":false})],"blendedInto":[makeQuery(id+"F1.opExtrude","CAP_FACE",FACE,{"disambiguationData":[OSD([sQuery(id+"F0.wireOp",EDGE,"E0.0"),sQuery(id+"F0.wireOp",EDGE,"E0.1"),subQ1,sQuery(id+"F0.wireOp",EDGE,"E0.3"),sQuery(id+"F0.wireOp",EDGE,"E0.4"),sQuery(id+"F0.wireOp",EDGE,"E0.5"),sQuery(id+"F0.wireOp",EDGE,"E0.6"),sQuery(id+"F0.wireOp",EDGE,"E0.7")])],"isStart":false})]});var subQ3=makeQuery(id+"F33.imprint","INTERSECT",VERTEX,{"disambiguationData":[OD(0.0)],"derivedFrom":[subQ2,subQ0]});Q12=makeQuery(id+"F33.imprint","IMPRINT",FACE,{"disambiguationData":[TD([[makeQuery(id+"F33.imprint","IMPRINT",EDGE,{"disambiguationData":[TD([[subQ3,-1.0]])],"derivedFrom":subQ0}),1.0]])]});}
            var Q13;
            {var subQ0=sQuery(id+"F33.wireOp",EDGE,"E54");var subQ1=sQuery(id+"F0.wireOp",EDGE,"E0.2");var subQ2=makeQuery(id+"F25.opFillet","BLEND_EDGE",EDGE,{"blendedFrom":[makeQuery(id+"F1.opExtrude","CAP_EDGE",EDGE,{"disambiguationData":[OSD([subQ1])],"isStart":false}),makeQuery(id+"F1.opExtrude","CAP_FACE",FACE,{"disambiguationData":[OSD([sQuery(id+"F0.wireOp",EDGE,"E0.0"),sQuery(id+"F0.wireOp",EDGE,"E0.1"),subQ1,sQuery(id+"F0.wireOp",EDGE,"E0.3"),sQuery(id+"F0.wireOp",EDGE,"E0.4"),sQuery(id+"F0.wireOp",EDGE,"E0.5"),sQuery(id+"F0.wireOp",EDGE,"E0.6"),sQuery(id+"F0.wireOp",EDGE,"E0.7")])],"isStart":false})],"blendedInto":[makeQuery(id+"F1.opExtrude","CAP_FACE",FACE,{"disambiguationData":[OSD([sQuery(id+"F0.wireOp",EDGE,"E0.0"),sQuery(id+"F0.wireOp",EDGE,"E0.1"),subQ1,sQuery(id+"F0.wireOp",EDGE,"E0.3"),sQuery(id+"F0.wireOp",EDGE,"E0.4"),sQuery(id+"F0.wireOp",EDGE,"E0.5"),sQuery(id+"F0.wireOp",EDGE,"E0.6"),sQuery(id+"F0.wireOp",EDGE,"E0.7")])],"isStart":false})]});var subQ3=makeQuery(id+"F33.imprint","INTERSECT",VERTEX,{"disambiguationData":[OD(0.0)],"derivedFrom":[subQ2,subQ0]});Q13=makeQuery(id+"F33.imprint","IMPRINT",FACE,{"disambiguationData":[TD([[makeQuery(id+"F33.imprint","IMPRINT",EDGE,{"disambiguationData":[TD([[subQ3,1.0]])],"derivedFrom":subQ0}),1.0]])]});}
            var Q14;
            {var subQ0=sQuery(id+"F33.wireOp",EDGE,"E55");var subQ1=sQuery(id+"F0.wireOp",EDGE,"E0.2");var subQ2=makeQuery(id+"F25.opFillet","BLEND_EDGE",EDGE,{"blendedFrom":[makeQuery(id+"F1.opExtrude","CAP_EDGE",EDGE,{"disambiguationData":[OSD([subQ1])],"isStart":false}),makeQuery(id+"F1.opExtrude","CAP_FACE",FACE,{"disambiguationData":[OSD([sQuery(id+"F0.wireOp",EDGE,"E0.0"),sQuery(id+"F0.wireOp",EDGE,"E0.1"),subQ1,sQuery(id+"F0.wireOp",EDGE,"E0.3"),sQuery(id+"F0.wireOp",EDGE,"E0.4"),sQuery(id+"F0.wireOp",EDGE,"E0.5"),sQuery(id+"F0.wireOp",EDGE,"E0.6"),sQuery(id+"F0.wireOp",EDGE,"E0.7")])],"isStart":false})],"blendedInto":[makeQuery(id+"F1.opExtrude","CAP_FACE",FACE,{"disambiguationData":[OSD([sQuery(id+"F0.wireOp",EDGE,"E0.0"),sQuery(id+"F0.wireOp",EDGE,"E0.1"),subQ1,sQuery(id+"F0.wireOp",EDGE,"E0.3"),sQuery(id+"F0.wireOp",EDGE,"E0.4"),sQuery(id+"F0.wireOp",EDGE,"E0.5"),sQuery(id+"F0.wireOp",EDGE,"E0.6"),sQuery(id+"F0.wireOp",EDGE,"E0.7")])],"isStart":false})]});var subQ3=makeQuery(id+"F33.imprint","INTERSECT",VERTEX,{"disambiguationData":[OD(0.0)],"derivedFrom":[subQ2,subQ0]});Q14=makeQuery(id+"F33.imprint","IMPRINT",FACE,{"disambiguationData":[TD([[makeQuery(id+"F33.imprint","IMPRINT",EDGE,{"disambiguationData":[TD([[subQ3,-1.0]])],"derivedFrom":subQ0}),1.0]])]});}
            var Q15;
            {var subQ0=sQuery(id+"F33.wireOp",EDGE,"E55");var subQ1=sQuery(id+"F0.wireOp",EDGE,"E0.2");var subQ2=makeQuery(id+"F25.opFillet","BLEND_EDGE",EDGE,{"blendedFrom":[makeQuery(id+"F1.opExtrude","CAP_EDGE",EDGE,{"disambiguationData":[OSD([subQ1])],"isStart":false}),makeQuery(id+"F1.opExtrude","CAP_FACE",FACE,{"disambiguationData":[OSD([sQuery(id+"F0.wireOp",EDGE,"E0.0"),sQuery(id+"F0.wireOp",EDGE,"E0.1"),subQ1,sQuery(id+"F0.wireOp",EDGE,"E0.3"),sQuery(id+"F0.wireOp",EDGE,"E0.4"),sQuery(id+"F0.wireOp",EDGE,"E0.5"),sQuery(id+"F0.wireOp",EDGE,"E0.6"),sQuery(id+"F0.wireOp",EDGE,"E0.7")])],"isStart":false})],"blendedInto":[makeQuery(id+"F1.opExtrude","CAP_FACE",FACE,{"disambiguationData":[OSD([sQuery(id+"F0.wireOp",EDGE,"E0.0"),sQuery(id+"F0.wireOp",EDGE,"E0.1"),subQ1,sQuery(id+"F0.wireOp",EDGE,"E0.3"),sQuery(id+"F0.wireOp",EDGE,"E0.4"),sQuery(id+"F0.wireOp",EDGE,"E0.5"),sQuery(id+"F0.wireOp",EDGE,"E0.6"),sQuery(id+"F0.wireOp",EDGE,"E0.7")])],"isStart":false})]});var subQ3=makeQuery(id+"F33.imprint","INTERSECT",VERTEX,{"disambiguationData":[OD(0.0)],"derivedFrom":[subQ2,subQ0]});Q15=makeQuery(id+"F33.imprint","IMPRINT",FACE,{"disambiguationData":[TD([[makeQuery(id+"F33.imprint","IMPRINT",EDGE,{"disambiguationData":[TD([[subQ3,1.0]])],"derivedFrom":subQ0}),1.0]])]});}
            extrude(context, id + "F34", {"entities" : qUnion([Q0, Q1, Q2, Q3, Q4, Q5, Q6, Q7, Q8, Q9, Q10, Q11, Q12, Q13, Q14, Q15]), "operationType" : NewBodyOperationType.REMOVE, "oppositeDirection" : true, "depth" : 20 * mm});
        }
        {
            var Q0;
            {var subQ0=sQuery(id+"F33.wireOp",EDGE,"E58");var subQ1=sQuery(id+"F0.wireOp",EDGE,"E0.4");var subQ2=makeQuery(id+"F25.opFillet","BLEND_EDGE",EDGE,{"blendedFrom":[makeQuery(id+"F1.opExtrude","CAP_EDGE",EDGE,{"disambiguationData":[OSD([subQ1])],"isStart":false}),makeQuery(id+"F1.opExtrude","CAP_FACE",FACE,{"disambiguationData":[OSD([sQuery(id+"F0.wireOp",EDGE,"E0.0"),sQuery(id+"F0.wireOp",EDGE,"E0.1"),sQuery(id+"F0.wireOp",EDGE,"E0.2"),sQuery(id+"F0.wireOp",EDGE,"E0.3"),subQ1,sQuery(id+"F0.wireOp",EDGE,"E0.5"),sQuery(id+"F0.wireOp",EDGE,"E0.6"),sQuery(id+"F0.wireOp",EDGE,"E0.7")])],"isStart":false})],"blendedInto":[makeQuery(id+"F1.opExtrude","CAP_FACE",FACE,{"disambiguationData":[OSD([sQuery(id+"F0.wireOp",EDGE,"E0.0"),sQuery(id+"F0.wireOp",EDGE,"E0.1"),sQuery(id+"F0.wireOp",EDGE,"E0.2"),sQuery(id+"F0.wireOp",EDGE,"E0.3"),subQ1,sQuery(id+"F0.wireOp",EDGE,"E0.5"),sQuery(id+"F0.wireOp",EDGE,"E0.6"),sQuery(id+"F0.wireOp",EDGE,"E0.7")])],"isStart":false})]});var subQ3=makeQuery(id+"F33.imprint","INTERSECT",VERTEX,{"disambiguationData":[OD(0.0)],"derivedFrom":[subQ2,subQ0]});Q0=makeQuery(id+"F33.imprint","IMPRINT",FACE,{"disambiguationData":[TD([[makeQuery(id+"F33.imprint","IMPRINT",EDGE,{"disambiguationData":[TD([[subQ3,-1.0]])],"derivedFrom":subQ0}),-1.0]])]});}
            var Q1;
            {var subQ0=sQuery(id+"F33.wireOp",EDGE,"E58");var subQ1=sQuery(id+"F0.wireOp",EDGE,"E0.4");var subQ2=makeQuery(id+"F25.opFillet","BLEND_EDGE",EDGE,{"blendedFrom":[makeQuery(id+"F1.opExtrude","CAP_EDGE",EDGE,{"disambiguationData":[OSD([subQ1])],"isStart":false}),makeQuery(id+"F1.opExtrude","CAP_FACE",FACE,{"disambiguationData":[OSD([sQuery(id+"F0.wireOp",EDGE,"E0.0"),sQuery(id+"F0.wireOp",EDGE,"E0.1"),sQuery(id+"F0.wireOp",EDGE,"E0.2"),sQuery(id+"F0.wireOp",EDGE,"E0.3"),subQ1,sQuery(id+"F0.wireOp",EDGE,"E0.5"),sQuery(id+"F0.wireOp",EDGE,"E0.6"),sQuery(id+"F0.wireOp",EDGE,"E0.7")])],"isStart":false})],"blendedInto":[makeQuery(id+"F1.opExtrude","CAP_FACE",FACE,{"disambiguationData":[OSD([sQuery(id+"F0.wireOp",EDGE,"E0.0"),sQuery(id+"F0.wireOp",EDGE,"E0.1"),sQuery(id+"F0.wireOp",EDGE,"E0.2"),sQuery(id+"F0.wireOp",EDGE,"E0.3"),subQ1,sQuery(id+"F0.wireOp",EDGE,"E0.5"),sQuery(id+"F0.wireOp",EDGE,"E0.6"),sQuery(id+"F0.wireOp",EDGE,"E0.7")])],"isStart":false})]});var subQ3=makeQuery(id+"F33.imprint","INTERSECT",VERTEX,{"disambiguationData":[OD(0.0)],"derivedFrom":[subQ2,subQ0]});Q1=makeQuery(id+"F33.imprint","IMPRINT",FACE,{"disambiguationData":[TD([[makeQuery(id+"F33.imprint","IMPRINT",EDGE,{"disambiguationData":[TD([[subQ3,1.0]])],"derivedFrom":subQ0}),-1.0]])]});}
            var Q2;
            {var subQ0=sQuery(id+"F33.wireOp",EDGE,"E59");var subQ1=sQuery(id+"F0.wireOp",EDGE,"E0.4");var subQ2=makeQuery(id+"F25.opFillet","BLEND_EDGE",EDGE,{"blendedFrom":[makeQuery(id+"F1.opExtrude","CAP_EDGE",EDGE,{"disambiguationData":[OSD([subQ1])],"isStart":false}),makeQuery(id+"F1.opExtrude","CAP_FACE",FACE,{"disambiguationData":[OSD([sQuery(id+"F0.wireOp",EDGE,"E0.0"),sQuery(id+"F0.wireOp",EDGE,"E0.1"),sQuery(id+"F0.wireOp",EDGE,"E0.2"),sQuery(id+"F0.wireOp",EDGE,"E0.3"),subQ1,sQuery(id+"F0.wireOp",EDGE,"E0.5"),sQuery(id+"F0.wireOp",EDGE,"E0.6"),sQuery(id+"F0.wireOp",EDGE,"E0.7")])],"isStart":false})],"blendedInto":[makeQuery(id+"F1.opExtrude","CAP_FACE",FACE,{"disambiguationData":[OSD([sQuery(id+"F0.wireOp",EDGE,"E0.0"),sQuery(id+"F0.wireOp",EDGE,"E0.1"),sQuery(id+"F0.wireOp",EDGE,"E0.2"),sQuery(id+"F0.wireOp",EDGE,"E0.3"),subQ1,sQuery(id+"F0.wireOp",EDGE,"E0.5"),sQuery(id+"F0.wireOp",EDGE,"E0.6"),sQuery(id+"F0.wireOp",EDGE,"E0.7")])],"isStart":false})]});var subQ3=makeQuery(id+"F33.imprint","INTERSECT",VERTEX,{"disambiguationData":[OD(0.0)],"derivedFrom":[subQ2,subQ0]});Q2=makeQuery(id+"F33.imprint","IMPRINT",FACE,{"disambiguationData":[TD([[makeQuery(id+"F33.imprint","IMPRINT",EDGE,{"disambiguationData":[TD([[subQ3,1.0]])],"derivedFrom":subQ0}),-1.0]])]});}
            var Q3;
            {var subQ0=sQuery(id+"F33.wireOp",EDGE,"E59");var subQ1=sQuery(id+"F0.wireOp",EDGE,"E0.4");var subQ2=makeQuery(id+"F25.opFillet","BLEND_EDGE",EDGE,{"blendedFrom":[makeQuery(id+"F1.opExtrude","CAP_EDGE",EDGE,{"disambiguationData":[OSD([subQ1])],"isStart":false}),makeQuery(id+"F1.opExtrude","CAP_FACE",FACE,{"disambiguationData":[OSD([sQuery(id+"F0.wireOp",EDGE,"E0.0"),sQuery(id+"F0.wireOp",EDGE,"E0.1"),sQuery(id+"F0.wireOp",EDGE,"E0.2"),sQuery(id+"F0.wireOp",EDGE,"E0.3"),subQ1,sQuery(id+"F0.wireOp",EDGE,"E0.5"),sQuery(id+"F0.wireOp",EDGE,"E0.6"),sQuery(id+"F0.wireOp",EDGE,"E0.7")])],"isStart":false})],"blendedInto":[makeQuery(id+"F1.opExtrude","CAP_FACE",FACE,{"disambiguationData":[OSD([sQuery(id+"F0.wireOp",EDGE,"E0.0"),sQuery(id+"F0.wireOp",EDGE,"E0.1"),sQuery(id+"F0.wireOp",EDGE,"E0.2"),sQuery(id+"F0.wireOp",EDGE,"E0.3"),subQ1,sQuery(id+"F0.wireOp",EDGE,"E0.5"),sQuery(id+"F0.wireOp",EDGE,"E0.6"),sQuery(id+"F0.wireOp",EDGE,"E0.7")])],"isStart":false})]});var subQ3=makeQuery(id+"F33.imprint","INTERSECT",VERTEX,{"disambiguationData":[OD(0.0)],"derivedFrom":[subQ2,subQ0]});Q3=makeQuery(id+"F33.imprint","IMPRINT",FACE,{"disambiguationData":[TD([[makeQuery(id+"F33.imprint","IMPRINT",EDGE,{"disambiguationData":[TD([[subQ3,-1.0]])],"derivedFrom":subQ0}),-1.0]])]});}
            var Q4;
            {var subQ0=sQuery(id+"F33.wireOp",EDGE,"E56.MirrorC");var subQ1=sQuery(id+"F0.wireOp",EDGE,"E0.6");var subQ2=makeQuery(id+"F25.opFillet","BLEND_EDGE",EDGE,{"blendedFrom":[makeQuery(id+"F1.opExtrude","CAP_EDGE",EDGE,{"disambiguationData":[OSD([subQ1])],"isStart":false}),makeQuery(id+"F1.opExtrude","CAP_FACE",FACE,{"disambiguationData":[OSD([sQuery(id+"F0.wireOp",EDGE,"E0.0"),sQuery(id+"F0.wireOp",EDGE,"E0.1"),sQuery(id+"F0.wireOp",EDGE,"E0.2"),sQuery(id+"F0.wireOp",EDGE,"E0.3"),sQuery(id+"F0.wireOp",EDGE,"E0.4"),sQuery(id+"F0.wireOp",EDGE,"E0.5"),subQ1,sQuery(id+"F0.wireOp",EDGE,"E0.7")])],"isStart":false})],"blendedInto":[makeQuery(id+"F1.opExtrude","CAP_FACE",FACE,{"disambiguationData":[OSD([sQuery(id+"F0.wireOp",EDGE,"E0.0"),sQuery(id+"F0.wireOp",EDGE,"E0.1"),sQuery(id+"F0.wireOp",EDGE,"E0.2"),sQuery(id+"F0.wireOp",EDGE,"E0.3"),sQuery(id+"F0.wireOp",EDGE,"E0.4"),sQuery(id+"F0.wireOp",EDGE,"E0.5"),subQ1,sQuery(id+"F0.wireOp",EDGE,"E0.7")])],"isStart":false})]});var subQ3=makeQuery(id+"F33.imprint","INTERSECT",VERTEX,{"disambiguationData":[OD(0.0)],"derivedFrom":[subQ2,subQ0]});Q4=makeQuery(id+"F33.imprint","IMPRINT",FACE,{"disambiguationData":[TD([[makeQuery(id+"F33.imprint","IMPRINT",EDGE,{"disambiguationData":[TD([[subQ3,-1.0]])],"derivedFrom":subQ0}),1.0]])]});}
            var Q5;
            {var subQ0=sQuery(id+"F33.wireOp",EDGE,"E56.MirrorC");var subQ1=sQuery(id+"F0.wireOp",EDGE,"E0.6");var subQ2=makeQuery(id+"F25.opFillet","BLEND_EDGE",EDGE,{"blendedFrom":[makeQuery(id+"F1.opExtrude","CAP_EDGE",EDGE,{"disambiguationData":[OSD([subQ1])],"isStart":false}),makeQuery(id+"F1.opExtrude","CAP_FACE",FACE,{"disambiguationData":[OSD([sQuery(id+"F0.wireOp",EDGE,"E0.0"),sQuery(id+"F0.wireOp",EDGE,"E0.1"),sQuery(id+"F0.wireOp",EDGE,"E0.2"),sQuery(id+"F0.wireOp",EDGE,"E0.3"),sQuery(id+"F0.wireOp",EDGE,"E0.4"),sQuery(id+"F0.wireOp",EDGE,"E0.5"),subQ1,sQuery(id+"F0.wireOp",EDGE,"E0.7")])],"isStart":false})],"blendedInto":[makeQuery(id+"F1.opExtrude","CAP_FACE",FACE,{"disambiguationData":[OSD([sQuery(id+"F0.wireOp",EDGE,"E0.0"),sQuery(id+"F0.wireOp",EDGE,"E0.1"),sQuery(id+"F0.wireOp",EDGE,"E0.2"),sQuery(id+"F0.wireOp",EDGE,"E0.3"),sQuery(id+"F0.wireOp",EDGE,"E0.4"),sQuery(id+"F0.wireOp",EDGE,"E0.5"),subQ1,sQuery(id+"F0.wireOp",EDGE,"E0.7")])],"isStart":false})]});var subQ3=makeQuery(id+"F33.imprint","INTERSECT",VERTEX,{"disambiguationData":[OD(0.0)],"derivedFrom":[subQ2,subQ0]});Q5=makeQuery(id+"F33.imprint","IMPRINT",FACE,{"disambiguationData":[TD([[makeQuery(id+"F33.imprint","IMPRINT",EDGE,{"disambiguationData":[TD([[subQ3,1.0]])],"derivedFrom":subQ0}),1.0]])]});}
            var Q6;
            {var subQ0=sQuery(id+"F33.wireOp",EDGE,"E57.MirrorC");var subQ1=sQuery(id+"F0.wireOp",EDGE,"E0.6");var subQ2=makeQuery(id+"F25.opFillet","BLEND_EDGE",EDGE,{"blendedFrom":[makeQuery(id+"F1.opExtrude","CAP_EDGE",EDGE,{"disambiguationData":[OSD([subQ1])],"isStart":false}),makeQuery(id+"F1.opExtrude","CAP_FACE",FACE,{"disambiguationData":[OSD([sQuery(id+"F0.wireOp",EDGE,"E0.0"),sQuery(id+"F0.wireOp",EDGE,"E0.1"),sQuery(id+"F0.wireOp",EDGE,"E0.2"),sQuery(id+"F0.wireOp",EDGE,"E0.3"),sQuery(id+"F0.wireOp",EDGE,"E0.4"),sQuery(id+"F0.wireOp",EDGE,"E0.5"),subQ1,sQuery(id+"F0.wireOp",EDGE,"E0.7")])],"isStart":false})],"blendedInto":[makeQuery(id+"F1.opExtrude","CAP_FACE",FACE,{"disambiguationData":[OSD([sQuery(id+"F0.wireOp",EDGE,"E0.0"),sQuery(id+"F0.wireOp",EDGE,"E0.1"),sQuery(id+"F0.wireOp",EDGE,"E0.2"),sQuery(id+"F0.wireOp",EDGE,"E0.3"),sQuery(id+"F0.wireOp",EDGE,"E0.4"),sQuery(id+"F0.wireOp",EDGE,"E0.5"),subQ1,sQuery(id+"F0.wireOp",EDGE,"E0.7")])],"isStart":false})]});var subQ3=makeQuery(id+"F33.imprint","INTERSECT",VERTEX,{"disambiguationData":[OD(0.0)],"derivedFrom":[subQ2,subQ0]});Q6=makeQuery(id+"F33.imprint","IMPRINT",FACE,{"disambiguationData":[TD([[makeQuery(id+"F33.imprint","IMPRINT",EDGE,{"disambiguationData":[TD([[subQ3,1.0]])],"derivedFrom":subQ0}),1.0]])]});}
            var Q7;
            {var subQ0=sQuery(id+"F33.wireOp",EDGE,"E57.MirrorC");var subQ1=sQuery(id+"F0.wireOp",EDGE,"E0.6");var subQ2=makeQuery(id+"F25.opFillet","BLEND_EDGE",EDGE,{"blendedFrom":[makeQuery(id+"F1.opExtrude","CAP_EDGE",EDGE,{"disambiguationData":[OSD([subQ1])],"isStart":false}),makeQuery(id+"F1.opExtrude","CAP_FACE",FACE,{"disambiguationData":[OSD([sQuery(id+"F0.wireOp",EDGE,"E0.0"),sQuery(id+"F0.wireOp",EDGE,"E0.1"),sQuery(id+"F0.wireOp",EDGE,"E0.2"),sQuery(id+"F0.wireOp",EDGE,"E0.3"),sQuery(id+"F0.wireOp",EDGE,"E0.4"),sQuery(id+"F0.wireOp",EDGE,"E0.5"),subQ1,sQuery(id+"F0.wireOp",EDGE,"E0.7")])],"isStart":false})],"blendedInto":[makeQuery(id+"F1.opExtrude","CAP_FACE",FACE,{"disambiguationData":[OSD([sQuery(id+"F0.wireOp",EDGE,"E0.0"),sQuery(id+"F0.wireOp",EDGE,"E0.1"),sQuery(id+"F0.wireOp",EDGE,"E0.2"),sQuery(id+"F0.wireOp",EDGE,"E0.3"),sQuery(id+"F0.wireOp",EDGE,"E0.4"),sQuery(id+"F0.wireOp",EDGE,"E0.5"),subQ1,sQuery(id+"F0.wireOp",EDGE,"E0.7")])],"isStart":false})]});var subQ3=makeQuery(id+"F33.imprint","INTERSECT",VERTEX,{"disambiguationData":[OD(0.0)],"derivedFrom":[subQ2,subQ0]});Q7=makeQuery(id+"F33.imprint","IMPRINT",FACE,{"disambiguationData":[TD([[makeQuery(id+"F33.imprint","IMPRINT",EDGE,{"disambiguationData":[TD([[subQ3,-1.0]])],"derivedFrom":subQ0}),1.0]])]});}
            var Q8;
            {var subQ0=sQuery(id+"F33.wireOp",EDGE,"E60.MirrorC");var subQ1=sQuery(id+"F0.wireOp",EDGE,"E0.0");var subQ2=makeQuery(id+"F25.opFillet","BLEND_EDGE",EDGE,{"blendedFrom":[makeQuery(id+"F1.opExtrude","CAP_EDGE",EDGE,{"disambiguationData":[OSD([subQ1])],"isStart":false}),makeQuery(id+"F1.opExtrude","CAP_FACE",FACE,{"disambiguationData":[OSD([subQ1,sQuery(id+"F0.wireOp",EDGE,"E0.1"),sQuery(id+"F0.wireOp",EDGE,"E0.2"),sQuery(id+"F0.wireOp",EDGE,"E0.3"),sQuery(id+"F0.wireOp",EDGE,"E0.4"),sQuery(id+"F0.wireOp",EDGE,"E0.5"),sQuery(id+"F0.wireOp",EDGE,"E0.6"),sQuery(id+"F0.wireOp",EDGE,"E0.7")])],"isStart":false})],"blendedInto":[makeQuery(id+"F1.opExtrude","CAP_FACE",FACE,{"disambiguationData":[OSD([subQ1,sQuery(id+"F0.wireOp",EDGE,"E0.1"),sQuery(id+"F0.wireOp",EDGE,"E0.2"),sQuery(id+"F0.wireOp",EDGE,"E0.3"),sQuery(id+"F0.wireOp",EDGE,"E0.4"),sQuery(id+"F0.wireOp",EDGE,"E0.5"),sQuery(id+"F0.wireOp",EDGE,"E0.6"),sQuery(id+"F0.wireOp",EDGE,"E0.7")])],"isStart":false})]});var subQ3=makeQuery(id+"F33.imprint","INTERSECT",VERTEX,{"disambiguationData":[OD(0.0)],"derivedFrom":[subQ2,subQ0]});Q8=makeQuery(id+"F33.imprint","IMPRINT",FACE,{"disambiguationData":[TD([[makeQuery(id+"F33.imprint","IMPRINT",EDGE,{"disambiguationData":[TD([[subQ3,1.0]])],"derivedFrom":subQ0}),1.0]])]});}
            var Q9;
            {var subQ0=sQuery(id+"F33.wireOp",EDGE,"E60.MirrorC");var subQ1=sQuery(id+"F0.wireOp",EDGE,"E0.0");var subQ2=makeQuery(id+"F25.opFillet","BLEND_EDGE",EDGE,{"blendedFrom":[makeQuery(id+"F1.opExtrude","CAP_EDGE",EDGE,{"disambiguationData":[OSD([subQ1])],"isStart":false}),makeQuery(id+"F1.opExtrude","CAP_FACE",FACE,{"disambiguationData":[OSD([subQ1,sQuery(id+"F0.wireOp",EDGE,"E0.1"),sQuery(id+"F0.wireOp",EDGE,"E0.2"),sQuery(id+"F0.wireOp",EDGE,"E0.3"),sQuery(id+"F0.wireOp",EDGE,"E0.4"),sQuery(id+"F0.wireOp",EDGE,"E0.5"),sQuery(id+"F0.wireOp",EDGE,"E0.6"),sQuery(id+"F0.wireOp",EDGE,"E0.7")])],"isStart":false})],"blendedInto":[makeQuery(id+"F1.opExtrude","CAP_FACE",FACE,{"disambiguationData":[OSD([subQ1,sQuery(id+"F0.wireOp",EDGE,"E0.1"),sQuery(id+"F0.wireOp",EDGE,"E0.2"),sQuery(id+"F0.wireOp",EDGE,"E0.3"),sQuery(id+"F0.wireOp",EDGE,"E0.4"),sQuery(id+"F0.wireOp",EDGE,"E0.5"),sQuery(id+"F0.wireOp",EDGE,"E0.6"),sQuery(id+"F0.wireOp",EDGE,"E0.7")])],"isStart":false})]});var subQ3=makeQuery(id+"F33.imprint","INTERSECT",VERTEX,{"disambiguationData":[OD(0.0)],"derivedFrom":[subQ2,subQ0]});Q9=makeQuery(id+"F33.imprint","IMPRINT",FACE,{"disambiguationData":[TD([[makeQuery(id+"F33.imprint","IMPRINT",EDGE,{"disambiguationData":[TD([[subQ3,-1.0]])],"derivedFrom":subQ0}),1.0]])]});}
            var Q10;
            {var subQ0=sQuery(id+"F33.wireOp",EDGE,"E61.MirrorC");var subQ1=sQuery(id+"F0.wireOp",EDGE,"E0.0");var subQ2=makeQuery(id+"F25.opFillet","BLEND_EDGE",EDGE,{"blendedFrom":[makeQuery(id+"F1.opExtrude","CAP_EDGE",EDGE,{"disambiguationData":[OSD([subQ1])],"isStart":false}),makeQuery(id+"F1.opExtrude","CAP_FACE",FACE,{"disambiguationData":[OSD([subQ1,sQuery(id+"F0.wireOp",EDGE,"E0.1"),sQuery(id+"F0.wireOp",EDGE,"E0.2"),sQuery(id+"F0.wireOp",EDGE,"E0.3"),sQuery(id+"F0.wireOp",EDGE,"E0.4"),sQuery(id+"F0.wireOp",EDGE,"E0.5"),sQuery(id+"F0.wireOp",EDGE,"E0.6"),sQuery(id+"F0.wireOp",EDGE,"E0.7")])],"isStart":false})],"blendedInto":[makeQuery(id+"F1.opExtrude","CAP_FACE",FACE,{"disambiguationData":[OSD([subQ1,sQuery(id+"F0.wireOp",EDGE,"E0.1"),sQuery(id+"F0.wireOp",EDGE,"E0.2"),sQuery(id+"F0.wireOp",EDGE,"E0.3"),sQuery(id+"F0.wireOp",EDGE,"E0.4"),sQuery(id+"F0.wireOp",EDGE,"E0.5"),sQuery(id+"F0.wireOp",EDGE,"E0.6"),sQuery(id+"F0.wireOp",EDGE,"E0.7")])],"isStart":false})]});var subQ3=makeQuery(id+"F33.imprint","INTERSECT",VERTEX,{"disambiguationData":[OD(0.0)],"derivedFrom":[subQ2,subQ0]});Q10=makeQuery(id+"F33.imprint","IMPRINT",FACE,{"disambiguationData":[TD([[makeQuery(id+"F33.imprint","IMPRINT",EDGE,{"disambiguationData":[TD([[subQ3,1.0]])],"derivedFrom":subQ0}),1.0]])]});}
            var Q11;
            {var subQ0=sQuery(id+"F33.wireOp",EDGE,"E61.MirrorC");var subQ1=sQuery(id+"F0.wireOp",EDGE,"E0.0");var subQ2=makeQuery(id+"F25.opFillet","BLEND_EDGE",EDGE,{"blendedFrom":[makeQuery(id+"F1.opExtrude","CAP_EDGE",EDGE,{"disambiguationData":[OSD([subQ1])],"isStart":false}),makeQuery(id+"F1.opExtrude","CAP_FACE",FACE,{"disambiguationData":[OSD([subQ1,sQuery(id+"F0.wireOp",EDGE,"E0.1"),sQuery(id+"F0.wireOp",EDGE,"E0.2"),sQuery(id+"F0.wireOp",EDGE,"E0.3"),sQuery(id+"F0.wireOp",EDGE,"E0.4"),sQuery(id+"F0.wireOp",EDGE,"E0.5"),sQuery(id+"F0.wireOp",EDGE,"E0.6"),sQuery(id+"F0.wireOp",EDGE,"E0.7")])],"isStart":false})],"blendedInto":[makeQuery(id+"F1.opExtrude","CAP_FACE",FACE,{"disambiguationData":[OSD([subQ1,sQuery(id+"F0.wireOp",EDGE,"E0.1"),sQuery(id+"F0.wireOp",EDGE,"E0.2"),sQuery(id+"F0.wireOp",EDGE,"E0.3"),sQuery(id+"F0.wireOp",EDGE,"E0.4"),sQuery(id+"F0.wireOp",EDGE,"E0.5"),sQuery(id+"F0.wireOp",EDGE,"E0.6"),sQuery(id+"F0.wireOp",EDGE,"E0.7")])],"isStart":false})]});var subQ3=makeQuery(id+"F33.imprint","INTERSECT",VERTEX,{"disambiguationData":[OD(0.0)],"derivedFrom":[subQ2,subQ0]});Q11=makeQuery(id+"F33.imprint","IMPRINT",FACE,{"disambiguationData":[TD([[makeQuery(id+"F33.imprint","IMPRINT",EDGE,{"disambiguationData":[TD([[subQ3,-1.0]])],"derivedFrom":subQ0}),1.0]])]});}
            var Q12;
            {var subQ0=sQuery(id+"F33.wireOp",EDGE,"E55");var subQ1=sQuery(id+"F0.wireOp",EDGE,"E0.2");var subQ2=makeQuery(id+"F25.opFillet","BLEND_EDGE",EDGE,{"blendedFrom":[makeQuery(id+"F1.opExtrude","CAP_EDGE",EDGE,{"disambiguationData":[OSD([subQ1])],"isStart":false}),makeQuery(id+"F1.opExtrude","CAP_FACE",FACE,{"disambiguationData":[OSD([sQuery(id+"F0.wireOp",EDGE,"E0.0"),sQuery(id+"F0.wireOp",EDGE,"E0.1"),subQ1,sQuery(id+"F0.wireOp",EDGE,"E0.3"),sQuery(id+"F0.wireOp",EDGE,"E0.4"),sQuery(id+"F0.wireOp",EDGE,"E0.5"),sQuery(id+"F0.wireOp",EDGE,"E0.6"),sQuery(id+"F0.wireOp",EDGE,"E0.7")])],"isStart":false})],"blendedInto":[makeQuery(id+"F1.opExtrude","CAP_FACE",FACE,{"disambiguationData":[OSD([sQuery(id+"F0.wireOp",EDGE,"E0.0"),sQuery(id+"F0.wireOp",EDGE,"E0.1"),subQ1,sQuery(id+"F0.wireOp",EDGE,"E0.3"),sQuery(id+"F0.wireOp",EDGE,"E0.4"),sQuery(id+"F0.wireOp",EDGE,"E0.5"),sQuery(id+"F0.wireOp",EDGE,"E0.6"),sQuery(id+"F0.wireOp",EDGE,"E0.7")])],"isStart":false})]});var subQ3=makeQuery(id+"F33.imprint","INTERSECT",VERTEX,{"disambiguationData":[OD(0.0)],"derivedFrom":[subQ2,subQ0]});Q12=makeQuery(id+"F33.imprint","IMPRINT",FACE,{"disambiguationData":[TD([[makeQuery(id+"F33.imprint","IMPRINT",EDGE,{"disambiguationData":[TD([[subQ3,-1.0]])],"derivedFrom":subQ0}),-1.0]])]});}
            var Q13;
            {var subQ0=sQuery(id+"F33.wireOp",EDGE,"E55");var subQ1=sQuery(id+"F0.wireOp",EDGE,"E0.2");var subQ2=makeQuery(id+"F25.opFillet","BLEND_EDGE",EDGE,{"blendedFrom":[makeQuery(id+"F1.opExtrude","CAP_EDGE",EDGE,{"disambiguationData":[OSD([subQ1])],"isStart":false}),makeQuery(id+"F1.opExtrude","CAP_FACE",FACE,{"disambiguationData":[OSD([sQuery(id+"F0.wireOp",EDGE,"E0.0"),sQuery(id+"F0.wireOp",EDGE,"E0.1"),subQ1,sQuery(id+"F0.wireOp",EDGE,"E0.3"),sQuery(id+"F0.wireOp",EDGE,"E0.4"),sQuery(id+"F0.wireOp",EDGE,"E0.5"),sQuery(id+"F0.wireOp",EDGE,"E0.6"),sQuery(id+"F0.wireOp",EDGE,"E0.7")])],"isStart":false})],"blendedInto":[makeQuery(id+"F1.opExtrude","CAP_FACE",FACE,{"disambiguationData":[OSD([sQuery(id+"F0.wireOp",EDGE,"E0.0"),sQuery(id+"F0.wireOp",EDGE,"E0.1"),subQ1,sQuery(id+"F0.wireOp",EDGE,"E0.3"),sQuery(id+"F0.wireOp",EDGE,"E0.4"),sQuery(id+"F0.wireOp",EDGE,"E0.5"),sQuery(id+"F0.wireOp",EDGE,"E0.6"),sQuery(id+"F0.wireOp",EDGE,"E0.7")])],"isStart":false})]});var subQ3=makeQuery(id+"F33.imprint","INTERSECT",VERTEX,{"disambiguationData":[OD(0.0)],"derivedFrom":[subQ2,subQ0]});Q13=makeQuery(id+"F33.imprint","IMPRINT",FACE,{"disambiguationData":[TD([[makeQuery(id+"F33.imprint","IMPRINT",EDGE,{"disambiguationData":[TD([[subQ3,1.0]])],"derivedFrom":subQ0}),-1.0]])]});}
            var Q14;
            {var subQ0=sQuery(id+"F33.wireOp",EDGE,"E54");var subQ1=sQuery(id+"F0.wireOp",EDGE,"E0.2");var subQ2=makeQuery(id+"F25.opFillet","BLEND_EDGE",EDGE,{"blendedFrom":[makeQuery(id+"F1.opExtrude","CAP_EDGE",EDGE,{"disambiguationData":[OSD([subQ1])],"isStart":false}),makeQuery(id+"F1.opExtrude","CAP_FACE",FACE,{"disambiguationData":[OSD([sQuery(id+"F0.wireOp",EDGE,"E0.0"),sQuery(id+"F0.wireOp",EDGE,"E0.1"),subQ1,sQuery(id+"F0.wireOp",EDGE,"E0.3"),sQuery(id+"F0.wireOp",EDGE,"E0.4"),sQuery(id+"F0.wireOp",EDGE,"E0.5"),sQuery(id+"F0.wireOp",EDGE,"E0.6"),sQuery(id+"F0.wireOp",EDGE,"E0.7")])],"isStart":false})],"blendedInto":[makeQuery(id+"F1.opExtrude","CAP_FACE",FACE,{"disambiguationData":[OSD([sQuery(id+"F0.wireOp",EDGE,"E0.0"),sQuery(id+"F0.wireOp",EDGE,"E0.1"),subQ1,sQuery(id+"F0.wireOp",EDGE,"E0.3"),sQuery(id+"F0.wireOp",EDGE,"E0.4"),sQuery(id+"F0.wireOp",EDGE,"E0.5"),sQuery(id+"F0.wireOp",EDGE,"E0.6"),sQuery(id+"F0.wireOp",EDGE,"E0.7")])],"isStart":false})]});var subQ3=makeQuery(id+"F33.imprint","INTERSECT",VERTEX,{"disambiguationData":[OD(0.0)],"derivedFrom":[subQ2,subQ0]});Q14=makeQuery(id+"F33.imprint","IMPRINT",FACE,{"disambiguationData":[TD([[makeQuery(id+"F33.imprint","IMPRINT",EDGE,{"disambiguationData":[TD([[subQ3,1.0]])],"derivedFrom":subQ0}),-1.0]])]});}
            var Q15;
            {var subQ0=sQuery(id+"F33.wireOp",EDGE,"E54");var subQ1=sQuery(id+"F0.wireOp",EDGE,"E0.2");var subQ2=makeQuery(id+"F25.opFillet","BLEND_EDGE",EDGE,{"blendedFrom":[makeQuery(id+"F1.opExtrude","CAP_EDGE",EDGE,{"disambiguationData":[OSD([subQ1])],"isStart":false}),makeQuery(id+"F1.opExtrude","CAP_FACE",FACE,{"disambiguationData":[OSD([sQuery(id+"F0.wireOp",EDGE,"E0.0"),sQuery(id+"F0.wireOp",EDGE,"E0.1"),subQ1,sQuery(id+"F0.wireOp",EDGE,"E0.3"),sQuery(id+"F0.wireOp",EDGE,"E0.4"),sQuery(id+"F0.wireOp",EDGE,"E0.5"),sQuery(id+"F0.wireOp",EDGE,"E0.6"),sQuery(id+"F0.wireOp",EDGE,"E0.7")])],"isStart":false})],"blendedInto":[makeQuery(id+"F1.opExtrude","CAP_FACE",FACE,{"disambiguationData":[OSD([sQuery(id+"F0.wireOp",EDGE,"E0.0"),sQuery(id+"F0.wireOp",EDGE,"E0.1"),subQ1,sQuery(id+"F0.wireOp",EDGE,"E0.3"),sQuery(id+"F0.wireOp",EDGE,"E0.4"),sQuery(id+"F0.wireOp",EDGE,"E0.5"),sQuery(id+"F0.wireOp",EDGE,"E0.6"),sQuery(id+"F0.wireOp",EDGE,"E0.7")])],"isStart":false})]});var subQ3=makeQuery(id+"F33.imprint","INTERSECT",VERTEX,{"disambiguationData":[OD(0.0)],"derivedFrom":[subQ2,subQ0]});Q15=makeQuery(id+"F33.imprint","IMPRINT",FACE,{"disambiguationData":[TD([[makeQuery(id+"F33.imprint","IMPRINT",EDGE,{"disambiguationData":[TD([[subQ3,-1.0]])],"derivedFrom":subQ0}),-1.0]])]});}
            extrude(context, id + "F35", {"entities" : qUnion([Q0, Q1, Q2, Q3, Q4, Q5, Q6, Q7, Q8, Q9, Q10, Q11, Q12, Q13, Q14, Q15]), "operationType" : NewBodyOperationType.REMOVE, "oppositeDirection" : true, "depth" : 2.5 * mm});
        }
        {
            var Q0;
            Q0=makeQuery(id+"F31.imprint","IMPRINT",FACE,{"disambiguationData":[TD([[makeQuery(id+"F31.imprint","IMPRINT",EDGE,{"derivedFrom":sQuery(id+"F31.wireOp",EDGE,"E53")}),1.0]])]});
            var Q1;
            Q1=makeQuery(id+"F31.imprint","IMPRINT",FACE,{"disambiguationData":[TD([[makeQuery(id+"F31.imprint","IMPRINT",EDGE,{"derivedFrom":sQuery(id+"F31.wireOp",EDGE,"E52")}),1.0]])]});
            extrude(context, id + "F36", {"entities" : qUnion([Q0, Q1]), "operationType" : NewBodyOperationType.ADD, "depth" : 15 * mm});
        }
        {
            var Q0;
            {var subQ4=sQuery(id+"F28.wireOp",EDGE,"E45.1");Q0=makeQuery(id+"F28.imprint","IMPRINT",FACE,{"disambiguationData":[TD([[makeQuery(id+"F28.imprint","IMPRINT",EDGE,{"derivedFrom":subQ4}),1.0]])]});}
            extrude(context, id + "F37", {"entities" : qUnion([Q0]), "operationType" : NewBodyOperationType.REMOVE, "oppositeDirection" : true, "depth" : 35 * mm});
        }
        {
            var Q0;
            Q0=makeQuery(id+"F37.boolean.opBoolean","COPY",EDGE,{"derivedFrom":makeQuery(id+"F37.opExtrude","SWEPT_EDGE",EDGE,{"disambiguationData":[OSD([sQuery(id+"F28.wireOp",EDGE,"E45.4"),sQuery(id+"F28.wireOp",EDGE,"E45.15")])]})});
            var Q1;
            Q1=makeQuery(id+"F37.boolean.opBoolean","COPY",EDGE,{"derivedFrom":makeQuery(id+"F37.opExtrude","SWEPT_EDGE",EDGE,{"disambiguationData":[OSD([sQuery(id+"F28.wireOp",EDGE,"E45.1"),sQuery(id+"F28.wireOp",EDGE,"E45.2")])]})});
            var Q2;
            Q2=makeQuery(id+"F37.boolean.opBoolean","COPY",EDGE,{"derivedFrom":makeQuery(id+"F37.opExtrude","SWEPT_EDGE",EDGE,{"disambiguationData":[OSD([sQuery(id+"F28.wireOp",EDGE,"E45.13"),sQuery(id+"F28.wireOp",EDGE,"E45.15")])]})});
            var Q3;
            Q3=makeQuery(id+"F37.boolean.opBoolean","COPY",EDGE,{"derivedFrom":makeQuery(id+"F37.opExtrude","SWEPT_EDGE",EDGE,{"disambiguationData":[OSD([sQuery(id+"F28.wireOp",EDGE,"E45.0"),sQuery(id+"F28.wireOp",EDGE,"E45.1")])]})});
            var Q4;
            Q4=makeQuery(id+"F37.boolean.opBoolean","COPY",EDGE,{"derivedFrom":makeQuery(id+"F37.opExtrude","SWEPT_EDGE",EDGE,{"disambiguationData":[OSD([sQuery(id+"F28.wireOp",EDGE,"E45.9"),sQuery(id+"F28.wireOp",EDGE,"E45.10")])]})});
            var Q5;
            Q5=makeQuery(id+"F37.boolean.opBoolean","COPY",EDGE,{"derivedFrom":makeQuery(id+"F37.opExtrude","SWEPT_EDGE",EDGE,{"disambiguationData":[OSD([sQuery(id+"F28.wireOp",EDGE,"E45.6"),sQuery(id+"F28.wireOp",EDGE,"E45.7")])]})});
            var Q6;
            Q6=makeQuery(id+"F37.boolean.opBoolean","COPY",EDGE,{"derivedFrom":makeQuery(id+"F37.opExtrude","SWEPT_EDGE",EDGE,{"disambiguationData":[OSD([sQuery(id+"F28.wireOp",EDGE,"E45.10"),sQuery(id+"F28.wireOp",EDGE,"E45.11")])]})});
            var Q7;
            Q7=makeQuery(id+"F37.boolean.opBoolean","COPY",EDGE,{"derivedFrom":makeQuery(id+"F37.opExtrude","SWEPT_EDGE",EDGE,{"disambiguationData":[OSD([sQuery(id+"F28.wireOp",EDGE,"E45.7"),sQuery(id+"F28.wireOp",EDGE,"E45.8")])]})});
            fillet(context, id + "F38", {"entities" : qUnion([Q0, Q1, Q2, Q3, Q4, Q5, Q6, Q7]), "radius" : 2.5 * mm, "tangentPropagation" : true, "allowEdgeOverflow" : false});
        }
    });
